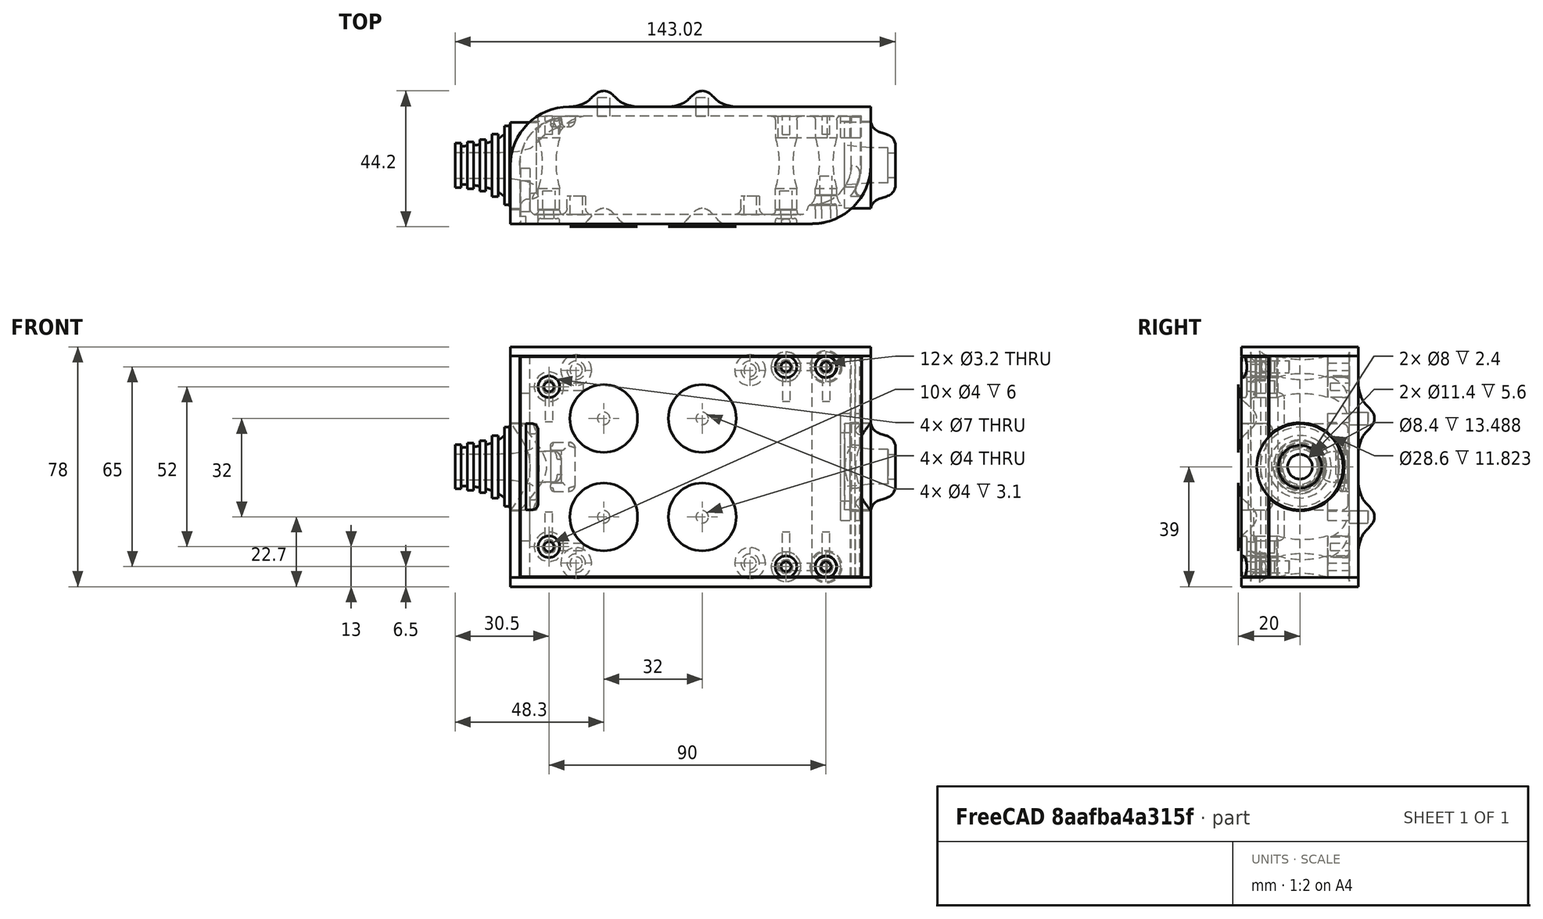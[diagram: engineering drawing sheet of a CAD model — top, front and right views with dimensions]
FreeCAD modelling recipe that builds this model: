
FCSTD DOCUMENT  (FreeCAD 0.19R0.19.2)
Label: enclosure_094
License: All rights reserved
LicenseURL: http://en.wikipedia.org/wiki/All_rights_reserved
objects: Part::Feature×72, Part::Revolution×72, Part::MultiFuse×52, Sketcher::SketchObject×29, Part::Fillet×22, Part::Cylinder×22, Part::Cut×19, Part::Extrusion×18, Part::Box×12, App::MeasureDistance×3
note: 318 computed .brp shape members not serialized (recipe doc carries the construction recipe); baked Part::Feature solids carry a one-line shape summary decoded from their .brp

FEATURE [Sketcher::SketchObject] Sketch  label="topSketch"
  FullyConstrained = true
  sketch-geometry (13):
    g0: LineSegment StartX=117 StartY=19 StartZ=0 EndX=117 EndY=38 EndZ=0
    g1: ArcOfCircle CenterX=98 CenterY=19 CenterZ=0 NormalX=0 NormalY=0 NormalZ=1 AngleXU=0 Radius=19 StartAngle=5.7297 EndAngle=6.28319
    g2: LineSegment StartX=0 StartY=3 StartZ=0 EndX=0 EndY=19 EndZ=0
    g3: LineSegment StartX=19 StartY=38 StartZ=0 EndX=117 EndY=38 EndZ=0
    g4: ArcOfCircle CenterX=19 CenterY=19 CenterZ=0 NormalX=0 NormalY=0 NormalZ=1 AngleXU=0 Radius=19 StartAngle=1.5708 EndAngle=3.14159
    g5: ArcOfCircle CenterX=19 CenterY=19 CenterZ=0 NormalX=0 NormalY=0 NormalZ=1 AngleXU=0 Radius=16 StartAngle=1.5708 EndAngle=3.14159
    g6: ArcOfCircle CenterX=98 CenterY=19 CenterZ=0 NormalX=0 NormalY=0 NormalZ=1 AngleXU=0 Radius=16 StartAngle=5.60905 EndAngle=6.28319
    g7: LineSegment StartX=114 StartY=19 StartZ=0 EndX=114 EndY=35 EndZ=0
    g8: LineSegment StartX=110.5 StartY=9.01251 StartZ=0 EndX=114.163 EndY=9.01251 EndZ=0
    g9: LineSegment StartX=114 StartY=35 StartZ=0 EndX=19 EndY=35 EndZ=0
    g10: LineSegment StartX=0 StartY=3 StartZ=0 EndX=0 EndY=0 EndZ=0
    g11: LineSegment StartX=3 StartY=0 StartZ=0 EndX=0 EndY=0 EndZ=0
    g12: LineSegment StartX=3 StartY=19 StartZ=0 EndX=3 EndY=0 EndZ=0
  constraints (33):
    c: Vertical(g0)
    c: Distance(g0) = 19
    c: Block(g0)
    c: Coincident(g1,g0)
    c: Block(g1)
    c: Vertical(g2)
    c: Block(g2)
    c: Coincident(g3,g0)
    c: Horizontal(g3)
    c: Distance(g3) = 98
    c: Coincident(g4,g3)
    c: Coincident(g4,g2)
    c: Block(g4)
    c: Coincident(g5,g4)
    c: Coincident(g6,g1)
    c: Block(g6)
    c: Block(g5)
    c: Coincident(g7,g6)
    c: Vertical(g7)
    c: Coincident(g8,g6)
    c: Coincident(g8,g1)
    c: Coincident(g9,g7)
    c: Coincident(g9,g5)
    c: Horizontal(g9)
    c: Tangent(g9,g5)
    c: Coincident(g10,g2)
    c: Distance(g10) = 3
    c: Vertical(g10)
    c: Coincident(g11,g10)
    c: Horizontal(g11)
    c: Coincident(g12,g5)
    c: Coincident(g12,g11)
    c: Vertical(g12)
FEATURE [Sketcher::SketchObject] Sketch001  label="bottomSketch"
  FullyConstrained = true
  sketch-geometry (32):
    g0: LineSegment StartX=3.3 StartY=-6.03275e-07 StartZ=0 EndX=98 EndY=-6.03275e-07 EndZ=0
    g1: ArcOfCircle CenterX=98 CenterY=19 CenterZ=0 NormalX=0 NormalY=0 NormalZ=1 AngleXU=0 Radius=19 StartAngle=4.71239 EndAngle=5.71103
    g2: LineSegment StartX=6.3 StartY=8 StartZ=0 EndX=3.3 EndY=8 EndZ=0
    g3: LineSegment StartX=3.3 StartY=8 StartZ=0 EndX=3.3 EndY=-6.03275e-07 EndZ=0
    g4: ArcOfCircle CenterX=8.3 CenterY=5 CenterZ=0 NormalX=0 NormalY=0 NormalZ=1 AngleXU=0 Radius=2 StartAngle=3.14159 EndAngle=4.71239
    g5: LineSegment StartX=6.3 StartY=8 StartZ=0 EndX=6.3 EndY=5 EndZ=0
    g6: ArcOfCircle CenterX=98 CenterY=19 CenterZ=0 NormalX=0 NormalY=0 NormalZ=1 AngleXU=0 Radius=12.7 StartAngle=4.71239 EndAngle=6.28319
    g7: LineSegment StartX=94.7 StartY=3 StartZ=0 EndX=8.3 EndY=3 EndZ=0
    g8-g12: Circle x5 (B-spline internal-alignment scaffolding for g13; pole/knot coordinates omitted)
    g13: BSplineCurve PolesCount=5 KnotsCount=3 Degree=3 IsPeriodic=0
    g14: GeomPoint X=98 Y=6.3 Z=0
    g15: GeomPoint X=96.3938 Y=4.71946 Z=0
    g16: GeomPoint X=94.7 Y=3 Z=0
    g17-g23: Circle x7 (B-spline internal-alignment scaffolding for g24; pole/knot coordinates omitted)
    g24: BSplineCurve PolesCount=7 KnotsCount=5 Degree=3 IsPeriodic=0
    g25-g29: GeomPoint x5 (B-spline internal-alignment scaffolding for g24; pole/knot coordinates omitted)
    g30: ArcOfCircle CenterX=98 CenterY=19 CenterZ=0 NormalX=0 NormalY=0 NormalZ=1 AngleXU=0 Radius=15.7 StartAngle=5.81226 EndAngle=6.28319
    g31: LineSegment StartX=110.7 StartY=19 StartZ=0 EndX=113.7 EndY=19 EndZ=0
  constraints (41):
    c: Horizontal(g0)
    c: Coincident(g1,g0)
    c: Block(g1)
    c: Horizontal(g2)
    c: Distance(g2) = 3
    c: Coincident(g3,g2)
    c: Vertical(g3)
    c: Coincident(g3,g0)
    c: Block(g4)
    c: Block(g2)
    c: Coincident(g5,g2)
    c: Coincident(g5,g4)
    c: Vertical(g5)
    c: Coincident(g6,g1)
    c: Block(g6)
    c: Coincident(g7,g4)
    c: Horizontal(g7)
    c: Block(g0)
    c: Block(g7)
    c: Block(g3)
    c: Coincident(g13,g6)
    c: Weight(g8) = 1
    c: Equal(g8, g9-g12) x4
    c: Coincident(g13,g7)
    c: InternalAlignment(g8-g12 -> g13) x5
    c: InternalAlignment(g14,g13)
    c: InternalAlignment(g15,g13)
    c: InternalAlignment(g16,g13)
    c: Block(g13)
    c: Weight(g17) = 1
    c: Equal(g17, g18-g23) x6
    c: Coincident(g24,g1)
    c: InternalAlignment(g17-g23 -> g24) x7
    c: InternalAlignment(g25-g29 -> g24) x5
    c: Block(g24)
    c: Coincident(g30,g24)
    c: Coincident(g31,g6)
    c: Coincident(g31,g30)
    c: Horizontal(g31)
    c: Block(g31)
    c: Block(g30)
FEATURE [Part::Extrusion] Extrude  label="top"
  Base = -> Sketch
  Dir = (0,0,1)
  DirMode = 2
  FaceMakerClass = Part::FaceMakerBullseye
  LengthFwd = 72
  LengthRev = 0
  Solid = true
  Symmetric = false
FEATURE [Part::Extrusion] Extrude001  label="bottom"
  Base = -> Sketch001
  Dir = (0,0,1)
  DirMode = 2
  FaceMakerClass = Part::FaceMakerBullseye
  LengthFwd = 71.4
  LengthRev = 0
  Placement = pos=(0,0,0.3) rot=(0,0,1;0rad)
  Solid = true
  Symmetric = false
FEATURE [Sketcher::SketchObject] Sketch002  label="topSketch001"
  FullyConstrained = true
  sketch-geometry (6):
    g0: LineSegment StartX=19 StartY=38 StartZ=0 EndX=117 EndY=38 EndZ=0
    g1: ArcOfCircle CenterX=19 CenterY=19 CenterZ=0 NormalX=0 NormalY=0 NormalZ=1 AngleXU=0 Radius=19 StartAngle=1.5708 EndAngle=3.14159
    g2: LineSegment StartX=117 StartY=38 StartZ=0 EndX=117 EndY=19 EndZ=0
    g3: LineSegment StartX=98 StartY=1.0161e-12 StartZ=0 EndX=5.22862e-06 EndY=1.0161e-12 EndZ=0
    g4: LineSegment StartX=5.22862e-06 StartY=19 StartZ=0 EndX=5.22862e-06 EndY=1.0161e-12 EndZ=0
    g5: ArcOfCircle CenterX=98 CenterY=19 CenterZ=0 NormalX=0 NormalY=0 NormalZ=1 AngleXU=0 Radius=19 StartAngle=4.71239 EndAngle=6.28319
  constraints (16):
    c: Horizontal(g0)
    c: Distance(g0) = 98
    c: Coincident(g1,g0)
    c: Block(g1)
    c: Coincident(g2,g0)
    c: Vertical(g2)
    c: Distance(g2) = 19
    c: Horizontal(g3)
    c: Coincident(g4,g1)
    c: Vertical(g4)
    c: Coincident(g3,g4)
    c: Block(g3)
    c: Coincident(g5,g2)
    c: Coincident(g5,g3)
    c: Block(g0)
    c: Block(g5)
FEATURE [Part::Extrusion] Extrude002  label="sideA"
  Base = -> Sketch002
  Dir = (0,0,1)
  DirMode = 2
  FaceMakerClass = Part::FaceMakerBullseye
  LengthFwd = 3
  LengthRev = 0
  Placement = pos=(0,0,-3) rot=(0,0,1;0rad)
  Solid = true
  Symmetric = false
FEATURE [Sketcher::SketchObject] Sketch003  label="topSketch002"
  FullyConstrained = true
  sketch-geometry (6):
    g0: LineSegment StartX=19 StartY=38 StartZ=0 EndX=117 EndY=38 EndZ=0
    g1: ArcOfCircle CenterX=19 CenterY=19 CenterZ=0 NormalX=0 NormalY=0 NormalZ=1 AngleXU=0 Radius=19 StartAngle=1.5708 EndAngle=3.14159
    g2: LineSegment StartX=117 StartY=38 StartZ=0 EndX=117 EndY=19 EndZ=0
    g3: LineSegment StartX=98 StartY=1.0161e-12 StartZ=0 EndX=5.22862e-06 EndY=1.0161e-12 EndZ=0
    g4: LineSegment StartX=5.22862e-06 StartY=19 StartZ=0 EndX=5.22862e-06 EndY=1.0161e-12 EndZ=0
    g5: ArcOfCircle CenterX=98 CenterY=19 CenterZ=0 NormalX=0 NormalY=0 NormalZ=1 AngleXU=0 Radius=19 StartAngle=4.71239 EndAngle=6.28319
  constraints (16):
    c: Horizontal(g0)
    c: Distance(g0) = 98
    c: Coincident(g1,g0)
    c: Block(g1)
    c: Coincident(g2,g0)
    c: Vertical(g2)
    c: Distance(g2) = 19
    c: Horizontal(g3)
    c: Coincident(g4,g1)
    c: Vertical(g4)
    c: Coincident(g3,g4)
    c: Block(g3)
    c: Coincident(g5,g2)
    c: Coincident(g5,g3)
    c: Block(g0)
    c: Block(g5)
FEATURE [Part::Extrusion] Extrude003  label="sideB"
  Base = -> Sketch003
  Dir = (0,0,1)
  DirMode = 2
  FaceMakerClass = Part::FaceMakerBullseye
  LengthFwd = 3
  LengthRev = 0
  Placement = pos=(0,0,72) rot=(0,0,1;0rad)
  Solid = true
  Symmetric = false
FEATURE [Sketcher::SketchObject] Sketch004
  FullyConstrained = true
  MapMode = 3
  Placement = pos=(0,0,0) rot=(1,0,0;1.5708rad)
  Support = -> [Extrude]
  sketch-geometry (8):
    g0: Circle CenterX=80.351 CenterY=-67.6202 CenterZ=0 NormalX=0 NormalY=0 NormalZ=1 AngleXU=0 Radius=2
    g1: Circle CenterX=80.351 CenterY=-67.6202 CenterZ=0 NormalX=0 NormalY=0 NormalZ=1 AngleXU=0 Radius=3
    g2: Circle CenterX=80.351 CenterY=-4.92017 CenterZ=0 NormalX=0 NormalY=0 NormalZ=1 AngleXU=0 Radius=2
    g3: Circle CenterX=80.351 CenterY=-4.92017 CenterZ=0 NormalX=0 NormalY=0 NormalZ=1 AngleXU=0 Radius=3
    g4: Circle CenterX=23.851 CenterY=-4.92017 CenterZ=0 NormalX=0 NormalY=0 NormalZ=1 AngleXU=0 Radius=2
    g5: Circle CenterX=23.851 CenterY=-4.92017 CenterZ=0 NormalX=0 NormalY=0 NormalZ=1 AngleXU=0 Radius=3
    g6: Circle CenterX=23.851 CenterY=-67.6202 CenterZ=0 NormalX=0 NormalY=0 NormalZ=1 AngleXU=0 Radius=2
    g7: Circle CenterX=23.851 CenterY=-67.6202 CenterZ=0 NormalX=0 NormalY=0 NormalZ=1 AngleXU=0 Radius=3
  constraints (8):
    c: Block(g3)
    c: Block(g2)
    c: Block(g1)
    c: Block(g0)
    c: Block(g6)
    c: Block(g7)
    c: Block(g4)
    c: Block(g5)
FEATURE [Part::Extrusion] Extrude004
  Base = -> Sketch004
  Dir = (0,-1,2e-16)
  DirMode = 2
  FaceMakerClass = Part::FaceMakerBullseye
  LengthFwd = 6
  LengthRev = 0
  Placement = pos=(0,9,0) rot=(0,0,1;0rad)
  Solid = true
  Symmetric = false
FEATURE [Sketcher::SketchObject] Sketch005
  FullyConstrained = true
  MapMode = 3
  Placement = pos=(0,0,0) rot=(1,0,0;1.5708rad)
  Support = -> [Extrude]
  sketch-geometry (8):
    g0: Circle CenterX=80.351 CenterY=-67.6202 CenterZ=0 NormalX=0 NormalY=0 NormalZ=1 AngleXU=0 Radius=3
    g1: Circle CenterX=80.351 CenterY=-4.92017 CenterZ=0 NormalX=0 NormalY=0 NormalZ=1 AngleXU=0 Radius=3
    g2: Circle CenterX=23.851 CenterY=-4.92017 CenterZ=0 NormalX=0 NormalY=0 NormalZ=1 AngleXU=0 Radius=3
    g3: Circle CenterX=23.851 CenterY=-67.6202 CenterZ=0 NormalX=0 NormalY=0 NormalZ=1 AngleXU=0 Radius=3
    g4: Circle CenterX=23.851 CenterY=-67.6202 CenterZ=0 NormalX=0 NormalY=0 NormalZ=1 AngleXU=0 Radius=5
    g5: Circle CenterX=80.351 CenterY=-67.6202 CenterZ=0 NormalX=0 NormalY=0 NormalZ=1 AngleXU=0 Radius=5
    g6: Circle CenterX=23.851 CenterY=-4.92017 CenterZ=0 NormalX=0 NormalY=0 NormalZ=1 AngleXU=0 Radius=5
    g7: Circle CenterX=80.351 CenterY=-4.92017 CenterZ=0 NormalX=0 NormalY=0 NormalZ=1 AngleXU=0 Radius=5
  constraints (8):
    c: Block(g1)
    c: Block(g0)
    c: Block(g3)
    c: Block(g2)
    c: Block(g5)
    c: Block(g4)
    c: Block(g6)
    c: Block(g7)
FEATURE [Part::Extrusion] Extrude005
  Base = -> Sketch005
  Dir = (0,-1,2e-16)
  DirMode = 2
  FaceMakerClass = Part::FaceMakerBullseye
  LengthFwd = 2
  LengthRev = 0
  Solid = true
  Symmetric = false
FEATURE [Sketcher::SketchObject] Sketch006
  FullyConstrained = true
  MapMode = 3
  Placement = pos=(0,0,0) rot=(1,0,0;1.5708rad)
  sketch-geometry (8):
    g0: Circle CenterX=80.351 CenterY=-67.6202 CenterZ=0 NormalX=0 NormalY=0 NormalZ=1 AngleXU=0 Radius=3
    g1: Circle CenterX=80.351 CenterY=-4.92017 CenterZ=0 NormalX=0 NormalY=0 NormalZ=1 AngleXU=0 Radius=3
    g2: Circle CenterX=23.851 CenterY=-4.92017 CenterZ=0 NormalX=0 NormalY=0 NormalZ=1 AngleXU=0 Radius=3
    g3: Circle CenterX=23.851 CenterY=-67.6202 CenterZ=0 NormalX=0 NormalY=0 NormalZ=1 AngleXU=0 Radius=3
    g4: Circle CenterX=23.851 CenterY=-67.6202 CenterZ=0 NormalX=0 NormalY=0 NormalZ=1 AngleXU=0 Radius=5
    g5: Circle CenterX=80.351 CenterY=-67.6202 CenterZ=0 NormalX=0 NormalY=0 NormalZ=1 AngleXU=0 Radius=5
    g6: Circle CenterX=23.851 CenterY=-4.92017 CenterZ=0 NormalX=0 NormalY=0 NormalZ=1 AngleXU=0 Radius=5
    g7: Circle CenterX=80.351 CenterY=-4.92017 CenterZ=0 NormalX=0 NormalY=0 NormalZ=1 AngleXU=0 Radius=5
  constraints (8):
    c: Block(g1)
    c: Block(g0)
    c: Block(g3)
    c: Block(g2)
    c: Block(g5)
    c: Block(g4)
    c: Block(g6)
    c: Block(g7)
FEATURE [Part::Extrusion] Extrude007
  Base = -> Sketch006
  Dir = (0,-1,2e-16)
  DirMode = 2
  FaceMakerClass = Part::FaceMakerBullseye
  LengthFwd = 2
  LengthRev = 0
  Solid = true
  Symmetric = false
FEATURE [Part::Fillet] Fillet
  Base = -> Extrude007
  Edges = 4 edges r=1.99: [Edge6,Edge12,Edge18,Edge24]
FEATURE [Part::Cut] Cut
  Base = -> Extrude005
  Placement = pos=(0,5,0) rot=(0,0,1;0rad)
  Tool = -> Fillet
FEATURE [Part::MultiFuse] Fusion  label="pCBScrews"
  Placement = pos=(-2.5,0,72.3) rot=(0,0,1;0rad)
  Shapes = -> [Extrude004,Cut]
FEATURE [App::MeasureDistance] Distance  label="Distance: 0.69 mm"
  Distance = 0.685967
  P1 = (24.0138,2.9647,0.3)
  P2 = (23.8901,3,-0.373787)
FEATURE [App::MeasureDistance] Distance001  label="Distance: 0.53 mm"
  Distance = 0.533607
  P1 = (80.2939,3,72.2334)
  P2 = (80.281,2.99661,71.7)
FEATURE [Part::Fillet] Fillet001
  Base = -> Extrude001
  Edges = 1 edges r=2.4: [Edge17]
FEATURE [Part::Fillet] Fillet002  label="bottom001"
  Base = -> Fillet001
  Edges = 1 edges r=2.4: [Edge36]
FEATURE [Part::Fillet] Fillet003  label="top001"
  Base = -> Extrude
  Edges = 1 edges r=2: [Edge1]
FEATURE [Sketcher::SketchObject] Sketch007
  FullyConstrained = true
  sketch-geometry (16):
    g0: LineSegment StartX=4 StartY=0 StartZ=0 EndX=4 EndY=2.4 EndZ=0
    g1: LineSegment StartX=4 StartY=2.4 StartZ=0 EndX=7 EndY=2.4 EndZ=0
    g2: LineSegment StartX=4 StartY=0 StartZ=0 EndX=5.7 EndY=0 EndZ=0
    g3: LineSegment StartX=5.7 StartY=0 StartZ=0 EndX=5.7 EndY=-5.6 EndZ=0
    g4-g8: Circle x5 (B-spline internal-alignment scaffolding for g9; pole/knot coordinates omitted)
    g9: BSplineCurve PolesCount=5 KnotsCount=3 Degree=3 IsPeriodic=0
    g10: GeomPoint X=7 Y=2.4 Z=0
    g11: GeomPoint X=10.4582 Y=-1.55472 Z=0
    g12: GeomPoint X=14 Y=-5.6 Z=0
    g13: LineSegment StartX=14 StartY=-5.6 StartZ=0 EndX=14 EndY=-14.1 EndZ=0
    g14: LineSegment StartX=14 StartY=-14.1 StartZ=0 EndX=6.5 EndY=-14.1 EndZ=0
    g15: LineSegment StartX=5.7 StartY=-5.6 StartZ=0 EndX=6.5 EndY=-14.1 EndZ=0
  constraints (28):
    c: Distance(g0) = 2.4
    c: Vertical(g0)
    c: Block(g0)
    c: Coincident(g1,g0)
    c: Horizontal(g1)
    c: Distance(g1) = 3
    c: Coincident(g2,g0)
    c: Horizontal(g2)
    c: Distance(g2) = 1.7
    c: Coincident(g3,g2)
    c: Vertical(g3)
    c: Distance(g3) = 5.6
    c: Coincident(g9,g1)
    c: Weight(g4) = 1
    c: Equal(g4, g5-g8) x4
    c: InternalAlignment(g4-g8 -> g9) x5
    c: InternalAlignment(g10,g9)
    c: InternalAlignment(g11,g9)
    c: InternalAlignment(g12,g9)
    c: Block(g9)
    c: Coincident(g13,g9)
    c: Vertical(g13)
    c: Distance(g13) = 8.5
    c: Coincident(g14,g13)
    c: Horizontal(g14)
    c: Distance(g14) = 7.5
    c: Coincident(g15,g3)
    c: Coincident(g15,g14)
FEATURE [Part::Feature] Face
  shape: bbox 10 x 16.5 x 2e-07 mm, 1 faces, 0 solids (baked)
FEATURE [Part::Revolution] Revolve  label="plugHousing"
  Angle = 360
  Axis = (0,1,0)
  Base = (0,0,0)
  FaceMakerClass = Part::FaceMakerBullseye
  Placement = pos=(0,0,36.15) rot=(0,0,1;0rad)
  Solid = false
  Source = -> Face
  Symmetric = false
FEATURE [Part::Feature] Face001
  shape: bbox 10 x 16.5 x 2e-07 mm, 1 faces, 0 solids (baked)
FEATURE [Part::Revolution] Revolve001  label="plugHousing001"
  Angle = 360
  Axis = (0,1,0)
  Base = (0,0,0)
  FaceMakerClass = Part::FaceMakerBullseye
  Placement = pos=(0,0,36.15) rot=(0,0,1;0rad)
  Solid = false
  Source = -> Face001
  Symmetric = false
FEATURE [Part::MultiFuse] Fusion001  label="plugHousing002"
  Placement = pos=(0,0,0) rot=(0,0,1;1.5708rad)
  Shapes = -> [Revolve001,Revolve]
FEATURE [Part::Feature] Face002
  shape: bbox 10 x 16.5 x 2e-07 mm, 1 faces, 0 solids (baked)
FEATURE [Part::Revolution] Revolve003  label="plugHousing005"
  Angle = 360
  Axis = (0,1,0)
  Base = (0,0,0)
  FaceMakerClass = Part::FaceMakerBullseye
  Placement = pos=(0,0,36.15) rot=(0,0,1;0rad)
  Solid = false
  Source = -> Face002
  Symmetric = false
FEATURE [Part::Feature] Face003
  shape: bbox 10 x 16.5 x 2e-07 mm, 1 faces, 0 solids (baked)
FEATURE [Part::Revolution] Revolve002  label="plugHousing003"
  Angle = 360
  Axis = (0,1,0)
  Base = (0,0,0)
  FaceMakerClass = Part::FaceMakerBullseye
  Placement = pos=(0,0,36.15) rot=(0,0,1;0rad)
  Solid = false
  Source = -> Face003
  Symmetric = false
FEATURE [Part::MultiFuse] Fusion002  label="plugHousing004"
  Placement = pos=(0,0,0) rot=(0,0,1;1.5708rad)
  Shapes = -> [Revolve002,Revolve003]
FEATURE [Part::MultiFuse] Fusion003  label="plugHousing006"
  Placement = pos=(0,19,0) rot=(0,0,1;3.14159rad)
  Shapes = -> [Fusion002,Fusion001]
FEATURE [Part::Feature] Face004
  shape: bbox 10 x 16.5 x 2e-07 mm, 1 faces, 0 solids (baked)
FEATURE [Part::Revolution] Revolve006  label="plugHousing010"
  Angle = 360
  Axis = (0,1,0)
  Base = (0,0,0)
  FaceMakerClass = Part::FaceMakerBullseye
  Placement = pos=(0,0,36.15) rot=(0,0,1;0rad)
  Solid = false
  Source = -> Face004
  Symmetric = false
FEATURE [Part::Feature] Face005
  shape: bbox 10 x 16.5 x 2e-07 mm, 1 faces, 0 solids (baked)
FEATURE [Part::Revolution] Revolve007  label="plugHousing011"
  Angle = 360
  Axis = (0,1,0)
  Base = (0,0,0)
  FaceMakerClass = Part::FaceMakerBullseye
  Placement = pos=(0,0,36.15) rot=(0,0,1;0rad)
  Solid = false
  Source = -> Face005
  Symmetric = false
FEATURE [Part::Feature] Face006
  shape: bbox 10 x 16.5 x 2e-07 mm, 1 faces, 0 solids (baked)
FEATURE [Part::Revolution] Revolve004  label="plugHousing007"
  Angle = 360
  Axis = (0,1,0)
  Base = (0,0,0)
  FaceMakerClass = Part::FaceMakerBullseye
  Placement = pos=(0,0,36.15) rot=(0,0,1;0rad)
  Solid = false
  Source = -> Face006
  Symmetric = false
FEATURE [Part::MultiFuse] Fusion004  label="plugHousing009"
  Placement = pos=(0,0,0) rot=(0,0,1;1.5708rad)
  Shapes = -> [Revolve004,Revolve007]
FEATURE [Part::Feature] Face007
  shape: bbox 10 x 16.5 x 2e-07 mm, 1 faces, 0 solids (baked)
FEATURE [Part::Revolution] Revolve005  label="plugHousing008"
  Angle = 360
  Axis = (0,1,0)
  Base = (0,0,0)
  FaceMakerClass = Part::FaceMakerBullseye
  Placement = pos=(0,0,36.15) rot=(0,0,1;0rad)
  Solid = false
  Source = -> Face007
  Symmetric = false
FEATURE [Part::MultiFuse] Fusion005  label="plugHousing012"
  Placement = pos=(0,0,0) rot=(0,0,1;1.5708rad)
  Shapes = -> [Revolve006,Revolve005]
FEATURE [Part::MultiFuse] Fusion006  label="plugHousing013"
  Placement = pos=(0,19,0) rot=(0,0,1;3.14159rad)
  Shapes = -> [Fusion005,Fusion004]
FEATURE [Part::MultiFuse] Fusion007  label="plugHousing014"
  Placement = pos=(122.621,0,-0.15) rot=(0,0,1;0rad)
  Shapes = -> [Fusion003,Fusion006]
FEATURE [Part::Cylinder] Cylinder002
  Angle = 360
  AttacherType = Attacher::AttachEngine3D
  Height = 20
  Placement = pos=(0,0,36.15) rot=(0,0,1;0rad)
  Radius = 4
FEATURE [Part::Cylinder] Cylinder003
  Angle = 360
  AttacherType = Attacher::AttachEngine3D
  Height = 10
  Placement = pos=(0,0,36.15) rot=(0,0,1;0rad)
  Radius = 4
FEATURE [Part::MultiFuse] Fusion009  label="removeToCreateHoleForPlugHousing"
  Placement = pos=(70,19,36.15) rot=(0,1,0;1.5708rad)
  Shapes = -> [Cylinder002,Cylinder003]
FEATURE [Part::Cylinder] Cylinder004
  Angle = 360
  AttacherType = Attacher::AttachEngine3D
  Height = 20
  Placement = pos=(0,0,36.15) rot=(0,0,1;0rad)
  Radius = 4
FEATURE [Part::Cylinder] Cylinder005
  Angle = 360
  AttacherType = Attacher::AttachEngine3D
  Height = 10
  Placement = pos=(0,0,36.15) rot=(0,0,1;0rad)
  Radius = 4
FEATURE [Part::MultiFuse] Fusion010  label="removeToCreateHoleForPlugHousing001"
  Placement = pos=(70,19,36.15) rot=(0,1,0;1.5708rad)
  Shapes = -> [Cylinder004,Cylinder005]
FEATURE [Part::Cut] Cut001
  Base = -> Fillet003
  Tool = -> Fusion010
FEATURE [Part::Cut] Cut002  label="Bottom"
  Base = -> Fillet002
  Tool = -> Fusion009
FEATURE [Part::Feature] Face008
  shape: bbox 10 x 16.5 x 2e-07 mm, 1 faces, 0 solids (baked)
FEATURE [Part::Revolution] Revolve011  label="plugHousing021"
  Angle = 360
  Axis = (0,1,0)
  Base = (0,0,0)
  FaceMakerClass = Part::FaceMakerBullseye
  Placement = pos=(0,0,36.15) rot=(0,0,1;0rad)
  Solid = false
  Source = -> Face008
  Symmetric = false
FEATURE [Part::Feature] Face009
  shape: bbox 10 x 16.5 x 2e-07 mm, 1 faces, 0 solids (baked)
FEATURE [Part::Revolution] Revolve012  label="plugHousing022"
  Angle = 360
  Axis = (0,1,0)
  Base = (0,0,0)
  FaceMakerClass = Part::FaceMakerBullseye
  Placement = pos=(0,0,36.15) rot=(0,0,1;0rad)
  Solid = false
  Source = -> Face009
  Symmetric = false
FEATURE [Part::Feature] Face010 .. Face013  x4 (patterned run collapsed; names and placements below)
  shape: bbox 10 x 16.5 x 2e-07 mm, 1 faces, 0 solids (baked)
FEATURE [Part::Revolution] Revolve015  label="plugHousing027"
  Angle = 360
  Axis = (0,1,0)
  Base = (0,0,0)
  FaceMakerClass = Part::FaceMakerBullseye
  Placement = pos=(0,0,36.15) rot=(0,0,1;0rad)
  Solid = false
  Source = -> Face013
  Symmetric = false
FEATURE [Part::Feature] Face014
  shape: bbox 10 x 16.5 x 2e-07 mm, 1 faces, 0 solids (baked)
FEATURE [Part::Feature] Face015
  shape: bbox 10 x 16.5 x 2e-07 mm, 1 faces, 0 solids (baked)
FEATURE [Part::Feature] Face016
  shape: bbox 10 x 16.5 x 2e-07 mm, 1 faces, 0 solids (baked)
FEATURE [Part::Revolution] Revolve019  label="plugHousing033"
  Angle = 360
  Axis = (0,1,0)
  Base = (0,0,0)
  FaceMakerClass = Part::FaceMakerBullseye
  Placement = pos=(0,0,36.15) rot=(0,0,1;0rad)
  Solid = false
  Source = -> Face016
  Symmetric = false
FEATURE [Part::Feature] Face017
  shape: bbox 10 x 16.5 x 2e-07 mm, 1 faces, 0 solids (baked)
FEATURE [Part::Revolution] Revolve020  label="plugHousing034"
  Angle = 360
  Axis = (0,1,0)
  Base = (0,0,0)
  FaceMakerClass = Part::FaceMakerBullseye
  Placement = pos=(0,0,36.15) rot=(0,0,1;0rad)
  Solid = false
  Source = -> Face017
  Symmetric = false
FEATURE [Part::Feature] Face018
  shape: bbox 10 x 16.5 x 2e-07 mm, 1 faces, 0 solids (baked)
FEATURE [Part::Revolution] Revolve016  label="plugHousing030"
  Angle = 360
  Axis = (0,1,0)
  Base = (0,0,0)
  FaceMakerClass = Part::FaceMakerBullseye
  Placement = pos=(0,0,36.15) rot=(0,0,1;0rad)
  Solid = false
  Source = -> Face018
  Symmetric = false
FEATURE [Part::MultiFuse] Fusion020  label="plugHousing038"
  Placement = pos=(0,0,0) rot=(0,0,1;1.5708rad)
  Shapes = -> [Revolve016,Revolve020]
FEATURE [Part::Feature] Face019
  shape: bbox 10 x 16.5 x 2e-07 mm, 1 faces, 0 solids (baked)
FEATURE [Part::Feature] Face020
  shape: bbox 10 x 16.5 x 2e-07 mm, 1 faces, 0 solids (baked)
FEATURE [Part::Revolution] Revolve017  label="plugHousing031"
  Angle = 360
  Axis = (0,1,0)
  Base = (0,0,0)
  FaceMakerClass = Part::FaceMakerBullseye
  Placement = pos=(0,0,36.15) rot=(0,0,1;0rad)
  Solid = false
  Source = -> Face020
  Symmetric = false
FEATURE [Part::MultiFuse] Fusion021  label="plugHousing039"
  Placement = pos=(0,0,0) rot=(0,0,1;1.5708rad)
  Shapes = -> [Revolve019,Revolve017]
FEATURE [Part::MultiFuse] Fusion023  label="plugHousing041"
  Placement = pos=(0,19,0) rot=(0,0,1;3.14159rad)
  Shapes = -> [Fusion021,Fusion020]
FEATURE [Part::Revolution] Revolve022  label="plugHousing043"
  Angle = 360
  Axis = (0,1,0)
  Base = (0,0,0)
  FaceMakerClass = Part::FaceMakerBullseye
  Placement = pos=(0,0,36.15) rot=(0,0,1;0rad)
  Solid = false
  Source = -> Face019
  Symmetric = false
FEATURE [Part::Feature] Face021
  shape: bbox 10 x 16.5 x 2e-07 mm, 1 faces, 0 solids (baked)
FEATURE [Part::Revolution] Revolve023  label="plugHousing044"
  Angle = 360
  Axis = (0,1,0)
  Base = (0,0,0)
  FaceMakerClass = Part::FaceMakerBullseye
  Placement = pos=(0,0,36.15) rot=(0,0,1;0rad)
  Solid = false
  Source = -> Face021
  Symmetric = false
FEATURE [Part::Feature] Face022
  shape: bbox 10 x 16.5 x 2e-07 mm, 1 faces, 0 solids (baked)
FEATURE [Part::Revolution] Revolve018  label="plugHousing032"
  Angle = 360
  Axis = (0,1,0)
  Base = (0,0,0)
  FaceMakerClass = Part::FaceMakerBullseye
  Placement = pos=(0,0,36.15) rot=(0,0,1;0rad)
  Solid = false
  Source = -> Face022
  Symmetric = false
FEATURE [Part::MultiFuse] Fusion022  label="plugHousing040"
  Placement = pos=(0,0,0) rot=(0,0,1;1.5708rad)
  Shapes = -> [Revolve018,Revolve023]
FEATURE [Part::Feature] Face023
  shape: bbox 10 x 16.5 x 2e-07 mm, 1 faces, 0 solids (baked)
FEATURE [Part::Revolution] Revolve021  label="plugHousing035"
  Angle = 360
  Axis = (0,1,0)
  Base = (0,0,0)
  FaceMakerClass = Part::FaceMakerBullseye
  Placement = pos=(0,0,36.15) rot=(0,0,1;0rad)
  Solid = false
  Source = -> Face023
  Symmetric = false
FEATURE [Part::MultiFuse] Fusion018  label="plugHousing036"
  Placement = pos=(0,0,0) rot=(0,0,1;1.5708rad)
  Shapes = -> [Revolve022,Revolve021]
FEATURE [Part::MultiFuse] Fusion019  label="plugHousing037"
  Placement = pos=(0,19,0) rot=(0,0,1;3.14159rad)
  Shapes = -> [Fusion018,Fusion022]
FEATURE [Part::MultiFuse] Fusion024  label="plugHousing042"
  Placement = pos=(122.621,0,-0.15) rot=(0,0,1;0rad)
  Shapes = -> [Fusion023,Fusion019]
FEATURE [Part::Cylinder] Cylinder006
  Angle = 360
  AttacherType = Attacher::AttachEngine3D
  Height = 20
  Placement = pos=(0,0,36.15) rot=(0,0,1;0rad)
  Radius = 14.3
FEATURE [Part::Cylinder] Cylinder007
  Angle = 360
  AttacherType = Attacher::AttachEngine3D
  Height = 10
  Placement = pos=(0,0,36.15) rot=(0,0,1;0rad)
  Radius = 4
FEATURE [Part::MultiFuse] Fusion026  label="removeToCreteHoleForPlugHousing"
  Placement = pos=(70,19,36) rot=(0,1,0;1.5708rad)
  Shapes = -> [Cylinder006,Cylinder007]
FEATURE [Part::Box] Box001  label="Cube001"
  AttacherType = Attacher::AttachEngine3D
  Height = 28
  Length = 3
  Placement = pos=(110.7,19,22) rot=(0,0,1;0rad)
  Width = 15.7
FEATURE [Part::Cut] Cut003  label="top002"
  Base = -> Cut001
  Tool = -> Fusion007
FEATURE [Part::Revolution] Revolve008  label="plugHousing015"
  Angle = 360
  Axis = (0,1,0)
  Base = (0,0,0)
  FaceMakerClass = Part::FaceMakerBullseye
  Placement = pos=(0,0,36.15) rot=(0,0,1;0rad)
  Solid = false
  Source = -> Face010
  Symmetric = false
FEATURE [Part::MultiFuse] Fusion013  label="plugHousing020"
  Placement = pos=(0,0,0) rot=(0,0,1;1.5708rad)
  Shapes = -> [Revolve008,Revolve012]
FEATURE [Part::Cut] Cut004  label="top003"
  Base = -> Cut003
  Placement = pos=(1,0,0) rot=(0,0,1;0rad)
  Tool = -> Fusion026
FEATURE [Part::Cylinder] Cylinder008
  Angle = 360
  AttacherType = Attacher::AttachEngine3D
  Height = 20
  Placement = pos=(0,0,36.15) rot=(0,0,1;0rad)
  Radius = 10.3
FEATURE [Part::Cylinder] Cylinder009
  Angle = 360
  AttacherType = Attacher::AttachEngine3D
  Height = 10
  Placement = pos=(0,0,36.15) rot=(0,0,1;0rad)
  Radius = 4
FEATURE [Part::MultiFuse] Fusion027  label="removeToCreteHoleForPlugHousing001"
  Placement = pos=(70,19,36) rot=(0,1,0;1.5708rad)
  Shapes = -> [Cylinder008,Cylinder009]
FEATURE [Part::Cut] Cut005  label="plugHousingTab"
  Base = -> Box001
  Tool = -> Fusion027
FEATURE [Part::MultiFuse] Fusion028  label="plugHousing045"
  Shapes = -> [Fusion024,Cut005]
FEATURE [Part::Box] Box002  label="Cube002"
  AttacherType = Attacher::AttachEngine3D
  Height = 28.8
  Length = 3
  Placement = pos=(107.3,28,21.6) rot=(0,0,1;0rad)
  Width = 7
FEATURE [Part::Box] Box003  label="Cube003"
  AttacherType = Attacher::AttachEngine3D
  Height = 3
  Length = 6.4
  Placement = pos=(107.3,28,18.6) rot=(0,0,1;0rad)
  Width = 7
FEATURE [Part::Box] Box004  label="Cube004"
  AttacherType = Attacher::AttachEngine3D
  Height = 3
  Length = 6.4
  Placement = pos=(107.3,28,50.4) rot=(0,0,1;0rad)
  Width = 7
FEATURE [Part::MultiFuse] Fusion029  label="plugHousingBracketHolder"
  Shapes = -> [Box004,Box002,Box003]
FEATURE [Part::Cylinder] Cylinder010
  Angle = 360
  AttacherType = Attacher::AttachEngine3D
  Height = 20
  Placement = pos=(0,0,36.15) rot=(0,0,1;0rad)
  Radius = 14.3
FEATURE [Part::Cylinder] Cylinder011
  Angle = 360
  AttacherType = Attacher::AttachEngine3D
  Height = 10
  Placement = pos=(0,0,36.15) rot=(0,0,1;0rad)
  Radius = 4
FEATURE [Part::MultiFuse] Fusion030  label="removeToCreteHoleForPlugHousing002"
  Placement = pos=(70,19,36) rot=(0,1,0;1.5708rad)
  Shapes = -> [Cylinder010,Cylinder011]
FEATURE [Part::Cut] Cut006  label="plugHousingBracketHolder001"
  Base = -> Fusion029
  Tool = -> Fusion030
FEATURE [Part::Cylinder] Cylinder012
  Angle = 360
  AttacherType = Attacher::AttachEngine3D
  Height = 20
  Placement = pos=(0,0,36.15) rot=(0,0,1;0rad)
  Radius = 7
FEATURE [Part::Cylinder] Cylinder013
  Angle = 360
  AttacherType = Attacher::AttachEngine3D
  Height = 10
  Placement = pos=(0,0,36.15) rot=(0,0,1;0rad)
  Radius = 4
FEATURE [Part::MultiFuse] Fusion032  label="removeToCreteHoleForPlugHousing003"
  Placement = pos=(70,19,36) rot=(0,1,0;1.5708rad)
  Shapes = -> [Cylinder012,Cylinder013]
FEATURE [Part::Cut] Cut007  label="bottom002"
  Base = -> Cut002
  Tool = -> Fusion032
FEATURE [Sketcher::SketchObject] Sketch008
  FullyConstrained = true
  sketch-geometry (54):
    g0: LineSegment StartX=-4.2 StartY=0 StartZ=0 EndX=-6.2 EndY=0 EndZ=0
    g1: LineSegment StartX=-14 StartY=-18 StartZ=0 EndX=-14 EndY=-26.5 EndZ=0
    g2: LineSegment StartX=-4.2 StartY=0 StartZ=0 EndX=-4.2 EndY=-13.4877 EndZ=0
    g3: Circle CenterX=-4.2 CenterY=-13.4877 CenterZ=0 NormalX=0 NormalY=0 NormalZ=1 AngleXU=0 Radius=1
    g4: Circle CenterX=-4.2 CenterY=-26.5 CenterZ=0 NormalX=0 NormalY=0 NormalZ=1 AngleXU=0 Radius=1
    g5: Circle CenterX=-8.2 CenterY=-26.5 CenterZ=0 NormalX=0 NormalY=0 NormalZ=1 AngleXU=0 Radius=1
    g6: BSplineCurve PolesCount=3 KnotsCount=2 Degree=2 IsPeriodic=0
    g7: GeomPoint X=-4.2 Y=-13.4877 Z=0
    g8: GeomPoint X=-8.2 Y=-26.5 Z=0
    g9: LineSegment StartX=-14 StartY=-26.5 StartZ=0 EndX=-8.2 EndY=-26.5 EndZ=0
    g10: LineSegment StartX=-10.15 StartY=-12 StartZ=0 EndX=-10.15 EndY=-14 EndZ=0
    g11: LineSegment StartX=-12.8401 StartY=-16 StartZ=0 EndX=-10.1571 EndY=-16 EndZ=0
    g12: LineSegment StartX=-10.15 StartY=-14 StartZ=0 EndX=-8.70761 EndY=-14 EndZ=0
    g13: LineSegment StartX=-12.8401 StartY=-16 StartZ=0 EndX=-12.8401 EndY=-17.6958 EndZ=0
    g14: LineSegment StartX=-10.15 StartY=-12 StartZ=0 EndX=-7.79258 EndY=-12 EndZ=0
    g15: Circle CenterX=-6.2215 CenterY=-2 CenterZ=0 NormalX=0 NormalY=0 NormalZ=1 AngleXU=0 Radius=1
    g16: Circle CenterX=-6.22762 CenterY=-2.58724 CenterZ=0 NormalX=0 NormalY=0 NormalZ=1 AngleXU=0 Radius=1
    g17: Circle CenterX=-6.32538 CenterY=-4 CenterZ=0 NormalX=0 NormalY=0 NormalZ=1 AngleXU=0 Radius=1
    g18: BSplineCurve PolesCount=3 KnotsCount=2 Degree=2 IsPeriodic=0
    g19: GeomPoint X=-6.2215 Y=-2 Z=0
    g20: GeomPoint X=-6.32538 Y=-4 Z=0
    g21: Circle CenterX=-6.48644 CenterY=-5.99526 CenterZ=0 NormalX=0 NormalY=0 NormalZ=1 AngleXU=0 Radius=1
    g22: Circle CenterX=-6.58486 CenterY=-6.99526 CenterZ=0 NormalX=0 NormalY=0 NormalZ=1 AngleXU=0 Radius=1
    g23: Circle CenterX=-6.77343 CenterY=-8 CenterZ=0 NormalX=0 NormalY=0 NormalZ=1 AngleXU=0 Radius=1
    g24: BSplineCurve PolesCount=3 KnotsCount=2 Degree=2 IsPeriodic=0
    g25: GeomPoint X=-6.48644 Y=-5.99526 Z=0
    g26: GeomPoint X=-6.77343 Y=-8 Z=0
    g27: Circle CenterX=-7.19003 CenterY=-10 CenterZ=0 NormalX=0 NormalY=0 NormalZ=1 AngleXU=0 Radius=1
    g28: Circle CenterX=-7.44407 CenterY=-11.0915 CenterZ=0 NormalX=0 NormalY=0 NormalZ=1 AngleXU=0 Radius=1
    g29: Circle CenterX=-7.79258 CenterY=-12 CenterZ=0 NormalX=0 NormalY=0 NormalZ=1 AngleXU=0 Radius=1
    g30: BSplineCurve PolesCount=3 KnotsCount=2 Degree=2 IsPeriodic=0
    g31: GeomPoint X=-7.19003 Y=-10 Z=0
    g32: GeomPoint X=-7.79258 Y=-12 Z=0
    g33: Circle CenterX=-8.70761 CenterY=-14 CenterZ=0 NormalX=0 NormalY=0 NormalZ=1 AngleXU=0 Radius=1
    g34: Circle CenterX=-9.33087 CenterY=-15.1837 CenterZ=0 NormalX=0 NormalY=0 NormalZ=1 AngleXU=0 Radius=1
    g35: Circle CenterX=-10.1571 CenterY=-16 CenterZ=0 NormalX=0 NormalY=0 NormalZ=1 AngleXU=0 Radius=1
    g36: BSplineCurve PolesCount=3 KnotsCount=2 Degree=2 IsPeriodic=0
    g37: GeomPoint X=-8.70761 Y=-14 Z=0
    g38: GeomPoint X=-10.1571 Y=-16 Z=0
    g39: Circle CenterX=-12.8401 CenterY=-17.6958 CenterZ=0 NormalX=0 NormalY=0 NormalZ=1 AngleXU=0 Radius=1
    g40: Circle CenterX=-13.3521 CenterY=-17.9027 CenterZ=0 NormalX=0 NormalY=0 NormalZ=1 AngleXU=0 Radius=1
    g41: Circle CenterX=-14 CenterY=-18 CenterZ=0 NormalX=0 NormalY=0 NormalZ=1 AngleXU=0 Radius=1
    g42: BSplineCurve PolesCount=3 KnotsCount=2 Degree=2 IsPeriodic=0
    g43: GeomPoint X=-12.8401 Y=-17.6958 Z=0
    g44: GeomPoint X=-14 Y=-18 Z=0
    g45: LineSegment StartX=-6.2 StartY=0 StartZ=0 EndX=-7.2 EndY=0 EndZ=0
    g46: LineSegment StartX=-7.2 StartY=0 StartZ=0 EndX=-7.2 EndY=-2 EndZ=0
    g47: LineSegment StartX=-7.2 StartY=-2 StartZ=0 EndX=-6.2215 EndY=-2 EndZ=0
    g48: LineSegment StartX=-6.32538 StartY=-4 StartZ=0 EndX=-7.65538 EndY=-4 EndZ=0
    g49: LineSegment StartX=-7.65538 StartY=-4 StartZ=0 EndX=-7.65538 EndY=-5.99526 EndZ=0
    g50: LineSegment StartX=-7.65538 StartY=-5.99526 StartZ=0 EndX=-6.48644 EndY=-5.99526 EndZ=0
    g51: LineSegment StartX=-6.77343 StartY=-8 StartZ=0 EndX=-8.43343 EndY=-8 EndZ=0
    g52: LineSegment StartX=-8.43343 StartY=-8 StartZ=0 EndX=-8.43343 EndY=-10 EndZ=0
    g53: LineSegment StartX=-8.43343 StartY=-10 StartZ=0 EndX=-7.19003 EndY=-10 EndZ=0
  constraints (112):
    c: Horizontal(g0)
    c: Distance(g0) = 2
    c: Block(g0)
    c: Vertical(g1)
    c: Coincident(g2,g0)
    c: Vertical(g2)
    c: Block(g2)
    c: Coincident(g6,g2)
    c: Weight(g3) = 1
    c: Equal(g3,g4)
    c: Equal(g3,g5)
    c: InternalAlignment(g3,g6)
    c: InternalAlignment(g4,g6)
    c: InternalAlignment(g5,g6)
    c: InternalAlignment(g7,g6)
    c: InternalAlignment(g8,g6)
    c: Block(g6)
    c: Coincident(g9,g1)
    c: Coincident(g9,g6)
    c: Horizontal(g9)
    c: Vertical(g10)
    c: Block(g10)
    c: Horizontal(g11)
    c: Block(g11)
    c: Coincident(g12,g10)
    c: Horizontal(g12)
    c: Block(g12)
    c: Coincident(g13,g11)
    c: Vertical(g13)
    c: Block(g13)
    c: Coincident(g14,g10)
    c: Horizontal(g14)
    c: Block(g14)
    c: Block(g9)
    c: Block(g1)
    c: Weight(g15) = 1
    c: Equal(g15,g16)
    c: Equal(g15,g17)
    c: InternalAlignment(g15,g18)
    c: InternalAlignment(g16,g18)
    c: InternalAlignment(g17,g18)
    c: InternalAlignment(g19,g18)
    c: InternalAlignment(g20,g18)
    c: Weight(g21) = 1
    c: Equal(g21,g22)
    c: Equal(g21,g23)
    c: InternalAlignment(g21,g24)
    c: InternalAlignment(g22,g24)
    c: InternalAlignment(g23,g24)
    c: InternalAlignment(g25,g24)
    c: InternalAlignment(g26,g24)
    c: Weight(g27) = 1
    c: Equal(g27,g28)
    c: Equal(g27,g29)
    c: Coincident(g30,g14)
    c: InternalAlignment(g27,g30)
    c: InternalAlignment(g28,g30)
    c: InternalAlignment(g29,g30)
    c: InternalAlignment(g31,g30)
    c: InternalAlignment(g32,g30)
    c: Coincident(g36,g12)
    c: Weight(g33) = 1
    c: Equal(g33,g34)
    c: Equal(g33,g35)
    c: Coincident(g36,g11)
    c: InternalAlignment(g33,g36)
    c: InternalAlignment(g34,g36)
    c: InternalAlignment(g35,g36)
    c: InternalAlignment(g37,g36)
    c: InternalAlignment(g38,g36)
    c: Coincident(g42,g13)
    c: Weight(g39) = 1
    c: Equal(g39,g40)
    c: Equal(g39,g41)
    c: Coincident(g42,g1)
    c: InternalAlignment(g39,g42)
    c: InternalAlignment(g40,g42)
    c: InternalAlignment(g41,g42)
    c: InternalAlignment(g43,g42)
    c: InternalAlignment(g44,g42)
    c: Block(g18)
    c: Block(g24)
    c: Block(g30)
    c: Block(g36)
    c: Block(g42)
    c: Horizontal(g45)
    c: Coincident(g45,g0)
    c: Vertical(g46)
    c: Coincident(g46,g45)
    c: Coincident(g47,g46)
    c: Coincident(g47,g18)
    c: Horizontal(g47)
    c: Block(g46)
    c: Coincident(g48,g18)
    c: Horizontal(g48)
    c: Distance(g48) = 1.33
    c: Vertical(g49)
    c: Coincident(g49,g48)
    c: Coincident(g50,g49)
    c: Coincident(g50,g24)
    c: Horizontal(g50)
    c: Tangent(g50,g22)
    c: Horizontal(g51)
    c: Coincident(g51,g24)
    c: Block(g51)
    c: Vertical(g52)
    c: Block(g52)
    c: Coincident(g52,g51)
    c: Coincident(g53,g52)
    c: Coincident(g53,g30)
    c: Horizontal(g53)
    c: Distance(g1) = 8.5
FEATURE [Part::Feature] Face024
  shape: bbox 9.8 x 26.5 x 2e-07 mm, 1 faces, 0 solids (baked)
FEATURE [Part::Revolution] Revolve024
  Angle = 360
  Axis = (0,1,0)
  Base = (0,0,0)
  FaceMakerClass = Part::FaceMakerBullseye
  Placement = pos=(0,0,0) rot=(0,0,1;1.5708rad)
  Solid = false
  Source = -> Face024
  Symmetric = false
FEATURE [Part::Feature] Face025
  shape: bbox 9.8 x 26.5 x 2e-07 mm, 1 faces, 0 solids (baked)
FEATURE [Part::Revolution] Revolve025
  Angle = 360
  Axis = (0,1,0)
  Base = (0,0,0)
  FaceMakerClass = Part::FaceMakerBullseye
  Placement = pos=(0,0,0) rot=(0,0,1;1.5708rad)
  Solid = false
  Source = -> Face025
  Symmetric = false
FEATURE [Part::MultiFuse] Fusion033
  Placement = pos=(-18,19,36) rot=(0,0,1;0rad)
  Shapes = -> [Revolve025,Revolve024]
FEATURE [Part::Cylinder] Cylinder014
  Angle = 360
  AttacherType = Attacher::AttachEngine3D
  Height = 20
  Placement = pos=(0,0,36.15) rot=(0,0,1;0rad)
  Radius = 14.3
FEATURE [Part::Cylinder] Cylinder015
  Angle = 360
  AttacherType = Attacher::AttachEngine3D
  Height = 10
  Placement = pos=(0,0,36.15) rot=(0,0,1;0rad)
  Radius = 4
FEATURE [Part::MultiFuse] Fusion034  label="removeToCreteHoleForPlugHousing004"
  Placement = pos=(-42,19,36) rot=(0,1,0;1.5708rad)
  Shapes = -> [Cylinder014,Cylinder015]
FEATURE [Part::Cut] Cut008  label="top004"
  Base = -> Cut004
  Placement = pos=(-1,0,0) rot=(0,0,1;0rad)
  Tool = -> Fusion034
FEATURE [Part::Box] Box005  label="Cube005"
  AttacherType = Attacher::AttachEngine3D
  Height = 28
  Length = 3
  Placement = pos=(110.7,19,22) rot=(0,0,1;0rad)
  Width = 15.7
FEATURE [Part::Cylinder] Cylinder016
  Angle = 360
  AttacherType = Attacher::AttachEngine3D
  Height = 10
  Placement = pos=(0,0,36.15) rot=(0,0,1;0rad)
  Radius = 4
FEATURE [Part::Cylinder] Cylinder017
  Angle = 360
  AttacherType = Attacher::AttachEngine3D
  Height = 20
  Placement = pos=(0,0,36.15) rot=(0,0,1;0rad)
  Radius = 10.3
FEATURE [Part::MultiFuse] Fusion035  label="removeToCreteHoleForPlugHousing005"
  Placement = pos=(70,19,36) rot=(0,1,0;1.5708rad)
  Shapes = -> [Cylinder017,Cylinder016]
FEATURE [Part::Cut] Cut009  label="plugHousingTab001"
  Base = -> Box005
  Placement = pos=(-107.4,-14,0) rot=(0,0,1;0rad)
  Tool = -> Fusion035
FEATURE [Part::Box] Box006  label="Cube006"
  AttacherType = Attacher::AttachEngine3D
  Height = 28
  Length = 3
  Placement = pos=(110.7,19,22) rot=(0,0,1;0rad)
  Width = 15.7
FEATURE [Part::Cylinder] Cylinder018
  Angle = 360
  AttacherType = Attacher::AttachEngine3D
  Height = 10
  Placement = pos=(0,0,36.15) rot=(0,0,1;0rad)
  Radius = 4
FEATURE [Part::Cylinder] Cylinder019
  Angle = 360
  AttacherType = Attacher::AttachEngine3D
  Height = 20
  Placement = pos=(0,0,36.15) rot=(0,0,1;0rad)
  Radius = 10.3
FEATURE [Part::MultiFuse] Fusion036  label="removeToCreteHoleForPlugHousing006"
  Placement = pos=(70,19,36) rot=(0,1,0;1.5708rad)
  Shapes = -> [Cylinder019,Cylinder018]
FEATURE [Part::Cut] Cut010  label="plugHousingTab002"
  Base = -> Box006
  Placement = pos=(-107.4,-14,0) rot=(0,0,1;0rad)
  Tool = -> Fusion036
FEATURE [Part::MultiFuse] Fusion037
  Placement = pos=(9.6,23,0) rot=(0,0,1;3.14159rad)
  Shapes = -> [Cut009,Cut010]
FEATURE [Part::Box] Box  label="Cube"
  AttacherType = Attacher::AttachEngine3D
  Height = 10
  Length = 3
  Placement = pos=(3.3,4,12) rot=(0,0,1;0rad)
  Width = 10
FEATURE [Part::Fillet] Fillet004
  Base = -> Fusion028
  Edges = 1 edges r=2: [Edge25]
FEATURE [Part::Fillet] Fillet005  label="plugHousing046"
  Base = -> Fillet004
  Edges = 1 edges r=2: [Edge8]
FEATURE [Part::Fillet] Fillet006
  Base = -> Box
  Edges = 1 edges r=2: [Edge11]
FEATURE [Part::Box] Box007  label="Cube007"
  AttacherType = Attacher::AttachEngine3D
  Height = 10
  Length = 3
  Placement = pos=(3.3,4,50) rot=(0,0,1;0rad)
  Width = 10
FEATURE [Part::Fillet] Fillet007
  Base = -> Box007
  Edges = 1 edges r=2: [Edge12]
FEATURE [Part::Box] Box008  label="Cube008"
  AttacherType = Attacher::AttachEngine3D
  Height = 28
  Length = 4
  Placement = pos=(5,0,22) rot=(0,0,1;0rad)
  Width = 10
FEATURE [Part::Fillet] Fillet008
  Base = -> Box008
  Edges = 1 edges r=1: [Edge7]
FEATURE [Part::Fillet] Fillet009
  Base = -> Fillet008
  Edges = 1 edges r=2: [Edge5]
FEATURE [Part::Fillet] Fillet010
  Base = -> Fillet009
  Edges = 1 edges r=2: [Edge2]
FEATURE [Sketcher::SketchObject] Sketch009  label="topSketch003"
  FullyConstrained = true
  sketch-geometry (4):
    g0: LineSegment StartX=16.8446 StartY=31.512 StartZ=0 EndX=16.3251 EndY=34.4666 EndZ=0
    g1: ArcOfCircle CenterX=19 CenterY=19.2524 CenterZ=0 NormalX=0 NormalY=0 NormalZ=1 AngleXU=0 Radius=15.4476 StartAngle=1.74483 EndAngle=2.72717
    g2: ArcOfCircle CenterX=19 CenterY=19.2524 CenterZ=0 NormalX=0 NormalY=0 NormalZ=1 AngleXU=0 Radius=12.4476 StartAngle=1.74483 EndAngle=2.73189
    g3: LineSegment StartX=4.86004 StartY=25.4725 StartZ=0 EndX=7.58253 EndY=24.2107 EndZ=0
  constraints (7):
    c: Block(g0)
    c: Coincident(g1,g0)
    c: Coincident(g2,g0)
    c: Coincident(g3,g1)
    c: Coincident(g3,g2)
    c: Block(g1)
    c: Block(g2)
FEATURE [Part::Extrusion] Extrude008
  Base = -> Sketch009
  Dir = (0,0,1)
  DirMode = 2
  FaceMakerClass = Part::FaceMakerBullseye
  LengthFwd = 10
  LengthRev = 0
  Placement = pos=(0,0,31) rot=(0,0,1;0rad)
  Solid = true
  Symmetric = false
FEATURE [Part::Cylinder] Cylinder020
  Angle = 360
  AttacherType = Attacher::AttachEngine3D
  Height = 20
  Placement = pos=(0,0,36.15) rot=(0,0,1;0rad)
  Radius = 8.2
FEATURE [Part::Cylinder] Cylinder021
  Angle = 360
  AttacherType = Attacher::AttachEngine3D
  Height = 10
  Placement = pos=(0,0,36.15) rot=(0,0,1;0rad)
  Radius = 4
FEATURE [Part::MultiFuse] Fusion038  label="removeToCreteHoleForPlugHousing007"
  Placement = pos=(-42,19,36) rot=(0,1,0;1.5708rad)
  Shapes = -> [Cylinder020,Cylinder021]
FEATURE [Part::Cut] Cut011
  Base = -> Extrude008
  Tool = -> Fusion038
FEATURE [Part::Fillet] Fillet011
  Base = -> Cut011
  Edges = 1 edges r=2: [Edge1]
FEATURE [Part::Fillet] Fillet012
  Base = -> Fillet011
  Edges = 1 edges r=2.5: [Edge1]
FEATURE [Part::Fillet] Fillet013
  Base = -> Fillet012
  Edges = 1 edges r=2.5: [Edge2]
FEATURE [Part::Box] Box010  label="Cube010"
  AttacherType = Attacher::AttachEngine3D
  Height = 16
  Length = 8
  Placement = pos=(12.7,31.52,28) rot=(0,0,1;0rad)
  Width = 4
FEATURE [Sketcher::SketchObject] Sketch010  label="topSketch004"
  FullyConstrained = true
  sketch-geometry (4):
    g0: LineSegment StartX=16.8446 StartY=31.512 StartZ=0 EndX=16.3251 EndY=34.4666 EndZ=0
    g1: ArcOfCircle CenterX=19 CenterY=19.2524 CenterZ=0 NormalX=0 NormalY=0 NormalZ=1 AngleXU=0 Radius=15.4476 StartAngle=1.74483 EndAngle=2.72717
    g2: ArcOfCircle CenterX=19 CenterY=19.2524 CenterZ=0 NormalX=0 NormalY=0 NormalZ=1 AngleXU=0 Radius=12.4476 StartAngle=1.74483 EndAngle=2.73189
    g3: LineSegment StartX=4.86004 StartY=25.4725 StartZ=0 EndX=7.58253 EndY=24.2107 EndZ=0
  constraints (7):
    c: Block(g0)
    c: Coincident(g1,g0)
    c: Coincident(g2,g0)
    c: Coincident(g3,g1)
    c: Coincident(g3,g2)
    c: Block(g1)
    c: Block(g2)
FEATURE [Part::Cylinder] Cylinder022
  Angle = 360
  AttacherType = Attacher::AttachEngine3D
  Height = 10
  Placement = pos=(0,0,36.15) rot=(0,0,1;0rad)
  Radius = 4
FEATURE [Sketcher::SketchObject] Sketch011  label="topSketch005"
  FullyConstrained = true
  sketch-geometry (4):
    g0: LineSegment StartX=16.8446 StartY=31.512 StartZ=0 EndX=16.3251 EndY=34.4666 EndZ=0
    g1: ArcOfCircle CenterX=19 CenterY=19.2524 CenterZ=0 NormalX=0 NormalY=0 NormalZ=1 AngleXU=0 Radius=15.4476 StartAngle=1.74483 EndAngle=2.72717
    g2: ArcOfCircle CenterX=19 CenterY=19.2524 CenterZ=0 NormalX=0 NormalY=0 NormalZ=1 AngleXU=0 Radius=12.4476 StartAngle=1.74483 EndAngle=2.73189
    g3: LineSegment StartX=4.86004 StartY=25.4725 StartZ=0 EndX=7.58253 EndY=24.2107 EndZ=0
  constraints (7):
    c: Block(g0)
    c: Coincident(g1,g0)
    c: Coincident(g2,g0)
    c: Coincident(g3,g1)
    c: Coincident(g3,g2)
    c: Block(g1)
    c: Block(g2)
FEATURE [Part::Extrusion] Extrude010
  Base = -> Sketch011
  Dir = (0,0,1)
  DirMode = 2
  FaceMakerClass = Part::FaceMakerBullseye
  LengthFwd = 10.6
  LengthRev = 0
  Placement = pos=(0,0,31) rot=(0,0,1;0rad)
  Solid = true
  Symmetric = false
FEATURE [Part::Cylinder] Cylinder023
  Angle = 360
  AttacherType = Attacher::AttachEngine3D
  Height = 20
  Placement = pos=(0,0,36.15) rot=(0,0,1;0rad)
  Radius = 8.2
FEATURE [Part::MultiFuse] Fusion039  label="removeToCreteHoleForPlugHousing008"
  Placement = pos=(-42,19,36) rot=(0,1,0;1.5708rad)
  Shapes = -> [Cylinder023,Cylinder022]
FEATURE [Part::Cut] Cut012
  Base = -> Extrude010
  Placement = pos=(0,0,-0.3) rot=(0,0,1;0rad)
  Tool = -> Fusion039
FEATURE [Part::Cut] Cut013
  Base = -> Box010
  Tool = -> Cut012
FEATURE [Part::Fillet] Fillet014
  Base = -> Cut013
  Edges = 1 edges r=0.7: [Edge13]
FEATURE [Part::Fillet] Fillet015
  Base = -> Fillet014
  Edges = 1 edges r=0.7: [Edge13]
FEATURE [Part::Fillet] Fillet016
  Base = -> Fillet015
  Edges = 1 edges r=0.7: [Edge16]
FEATURE [Part::Fillet] Fillet017
  Base = -> Fillet016
  Edges = 1 edges r=0.7: [Edge11]
FEATURE [Part::Fillet] Fillet018
  Base = -> Fillet017
  Edges = 1 edges r=0.7: [Edge10]
FEATURE [Part::Fillet] Fillet019
  Base = -> Fillet018
  Edges = 1 edges r=1.2: [Edge5]
FEATURE [Part::Fillet] Fillet020
  Base = -> Fillet019
  Edges = 1 edges r=1.2: [Edge12]
FEATURE [Part::Fillet] Fillet021
  Base = -> Fillet020
  Edges = 1 edges r=2: [Edge1]
  Placement = pos=(0.3,0,0) rot=(0,0,1;0rad)
FEATURE [Part::MultiFuse] Fusion040  label="top005"
  Shapes = -> [Cut008,Fillet021]
FEATURE [Part::MultiFuse] Fusion041  label="wireHolder"
  Shapes = -> [Fusion033,Fillet013]
FEATURE [Part::MultiFuse] Fusion042
  Shapes = -> [Fillet007,Fusion041]
FEATURE [Part::MultiFuse] Fusion043  label="wireHolder001"
  Shapes = -> [Fusion042,Fillet010]
FEATURE [Part::MultiFuse] Fusion044  label="wireHolder002"
  Shapes = -> [Fillet006,Fusion037,Fusion043]
FEATURE [Part::Feature] Face026
  shape: bbox 11 x 6 x 2e-07 mm, 1 faces, 0 solids (baked)
FEATURE [Part::Revolution] Revolve026
  Angle = 360
  Axis = (0,1,0)
  Base = (0,0,0)
  FaceMakerClass = Part::FaceMakerBullseye
  Placement = pos=(30.3,-1,19.7) rot=(0,0,1;0rad)
  Solid = false
  Source = -> Face026
  Symmetric = false
FEATURE [Sketcher::SketchObject] Sketch013  label="topSketch006"
  FullyConstrained = true
  sketch-geometry (13):
    g0: LineSegment StartX=117 StartY=19 StartZ=0 EndX=117 EndY=38 EndZ=0
    g1: ArcOfCircle CenterX=98 CenterY=19 CenterZ=0 NormalX=0 NormalY=0 NormalZ=1 AngleXU=0 Radius=19 StartAngle=5.7297 EndAngle=6.28319
    g2: LineSegment StartX=0 StartY=3 StartZ=0 EndX=0 EndY=19 EndZ=0
    g3: LineSegment StartX=19 StartY=38 StartZ=0 EndX=117 EndY=38 EndZ=0
    g4: ArcOfCircle CenterX=19 CenterY=19 CenterZ=0 NormalX=0 NormalY=0 NormalZ=1 AngleXU=0 Radius=19 StartAngle=1.5708 EndAngle=3.14159
    g5: ArcOfCircle CenterX=19 CenterY=19 CenterZ=0 NormalX=0 NormalY=0 NormalZ=1 AngleXU=0 Radius=16 StartAngle=1.5708 EndAngle=3.14159
    g6: ArcOfCircle CenterX=98 CenterY=19 CenterZ=0 NormalX=0 NormalY=0 NormalZ=1 AngleXU=0 Radius=16 StartAngle=5.60905 EndAngle=6.28319
    g7: LineSegment StartX=114 StartY=19 StartZ=0 EndX=114 EndY=35 EndZ=0
    g8: LineSegment StartX=110.5 StartY=9.01251 StartZ=0 EndX=114.163 EndY=9.01251 EndZ=0
    g9: LineSegment StartX=114 StartY=35 StartZ=0 EndX=19 EndY=35 EndZ=0
    g10: LineSegment StartX=0 StartY=3 StartZ=0 EndX=0 EndY=0 EndZ=0
    g11: LineSegment StartX=3 StartY=0 StartZ=0 EndX=0 EndY=0 EndZ=0
    g12: LineSegment StartX=3 StartY=19 StartZ=0 EndX=3 EndY=0 EndZ=0
  constraints (33):
    c: Vertical(g0)
    c: Distance(g0) = 19
    c: Block(g0)
    c: Coincident(g1,g0)
    c: Block(g1)
    c: Vertical(g2)
    c: Block(g2)
    c: Coincident(g3,g0)
    c: Horizontal(g3)
    c: Distance(g3) = 98
    c: Coincident(g4,g3)
    c: Coincident(g4,g2)
    c: Block(g4)
    c: Coincident(g5,g4)
    c: Coincident(g6,g1)
    c: Block(g6)
    c: Block(g5)
    c: Coincident(g7,g6)
    c: Vertical(g7)
    c: Coincident(g8,g6)
    c: Coincident(g8,g1)
    c: Coincident(g9,g7)
    c: Coincident(g9,g5)
    c: Horizontal(g9)
    c: Tangent(g9,g5)
    c: Coincident(g10,g2)
    c: Distance(g10) = 3
    c: Vertical(g10)
    c: Coincident(g11,g10)
    c: Horizontal(g11)
    c: Coincident(g12,g5)
    c: Coincident(g12,g11)
    c: Vertical(g12)
FEATURE [Part::Extrusion] Extrude011  label="top006"
  Base = -> Sketch013
  Dir = (0,0,1)
  DirMode = 2
  FaceMakerClass = Part::FaceMakerBullseye
  LengthFwd = 72
  LengthRev = 0
  Solid = true
  Symmetric = false
FEATURE [Sketcher::SketchObject] Sketch014
  FullyConstrained = true
  MapMode = 3
  Placement = pos=(0,0,0) rot=(1,0,0;1.5708rad)
  Support = -> [Extrude011]
  sketch-geometry (8):
    g0: Circle CenterX=80.351 CenterY=-67.6202 CenterZ=0 NormalX=0 NormalY=0 NormalZ=1 AngleXU=0 Radius=2
    g1: Circle CenterX=80.351 CenterY=-67.6202 CenterZ=0 NormalX=0 NormalY=0 NormalZ=1 AngleXU=0 Radius=3
    g2: Circle CenterX=80.351 CenterY=-4.92017 CenterZ=0 NormalX=0 NormalY=0 NormalZ=1 AngleXU=0 Radius=2
    g3: Circle CenterX=80.351 CenterY=-4.92017 CenterZ=0 NormalX=0 NormalY=0 NormalZ=1 AngleXU=0 Radius=3
    g4: Circle CenterX=23.851 CenterY=-4.92017 CenterZ=0 NormalX=0 NormalY=0 NormalZ=1 AngleXU=0 Radius=2
    g5: Circle CenterX=23.851 CenterY=-4.92017 CenterZ=0 NormalX=0 NormalY=0 NormalZ=1 AngleXU=0 Radius=3
    g6: Circle CenterX=23.851 CenterY=-67.6202 CenterZ=0 NormalX=0 NormalY=0 NormalZ=1 AngleXU=0 Radius=2
    g7: Circle CenterX=23.851 CenterY=-67.6202 CenterZ=0 NormalX=0 NormalY=0 NormalZ=1 AngleXU=0 Radius=3
  constraints (8):
    c: Block(g3)
    c: Block(g2)
    c: Block(g1)
    c: Block(g0)
    c: Block(g6)
    c: Block(g7)
    c: Block(g4)
    c: Block(g5)
FEATURE [Part::Feature] Face027
  shape: bbox 11 x 6 x 2e-07 mm, 1 faces, 0 solids (baked)
FEATURE [Part::Revolution] Revolve027
  Angle = 360
  Axis = (0,1,0)
  Base = (0,0,0)
  FaceMakerClass = Part::FaceMakerBullseye
  Placement = pos=(30.3,-1,51.7) rot=(0,0,1;0rad)
  Solid = false
  Source = -> Face027
  Symmetric = false
FEATURE [Part::Feature] Face028
  shape: bbox 11 x 6 x 2e-07 mm, 1 faces, 0 solids (baked)
FEATURE [Part::Revolution] Revolve028
  Angle = 360
  Axis = (0,1,0)
  Base = (0,0,0)
  FaceMakerClass = Part::FaceMakerBullseye
  Placement = pos=(62.3,-1,19.7) rot=(0,0,1;0rad)
  Solid = false
  Source = -> Face028
  Symmetric = false
FEATURE [Part::Feature] Face029
  shape: bbox 11 x 6 x 2e-07 mm, 1 faces, 0 solids (baked)
FEATURE [Part::Revolution] Revolve029
  Angle = 360
  Axis = (0,1,0)
  Base = (0,0,0)
  FaceMakerClass = Part::FaceMakerBullseye
  Placement = pos=(62.3,-1,51.7) rot=(0,0,1;0rad)
  Solid = false
  Source = -> Face029
  Symmetric = false
FEATURE [Part::Feature] Wire
  shape: bbox 11 x 5.2 x 2e-07 mm, 0 faces, 0 solids (baked)
FEATURE [Part::Revolution] Revolve030
  Angle = 360
  Axis = (0,1,0)
  Base = (0,0,0)
  FaceMakerClass = Part::FaceMakerBullseye
  Placement = pos=(30.3,38,19.7) rot=(0,0,1;0rad)
  Solid = true
  Source = -> Wire
  Symmetric = false
FEATURE [Part::Feature] Wire001
  shape: bbox 11 x 5.2 x 2e-07 mm, 0 faces, 0 solids (baked)
FEATURE [Part::Revolution] Revolve031
  Angle = 360
  Axis = (0,1,0)
  Base = (0,0,0)
  FaceMakerClass = Part::FaceMakerBullseye
  Placement = pos=(30.3,38,51.7) rot=(0,0,1;0rad)
  Solid = true
  Source = -> Wire001
  Symmetric = false
FEATURE [Part::Feature] Wire002
  shape: bbox 11 x 5.2 x 2e-07 mm, 0 faces, 0 solids (baked)
FEATURE [Part::Revolution] Revolve032
  Angle = 360
  Axis = (0,1,0)
  Base = (0,0,0)
  FaceMakerClass = Part::FaceMakerBullseye
  Placement = pos=(62.3,38,51.7) rot=(0,0,1;0rad)
  Solid = true
  Source = -> Wire002
  Symmetric = false
FEATURE [Part::Feature] Wire003
  shape: bbox 11 x 5.2 x 2e-07 mm, 0 faces, 0 solids (baked)
FEATURE [Part::Revolution] Revolve033
  Angle = 360
  Axis = (0,1,0)
  Base = (0,0,0)
  FaceMakerClass = Part::FaceMakerBullseye
  Placement = pos=(62.3,38,19.7) rot=(0,0,1;0rad)
  Solid = true
  Source = -> Wire003
  Symmetric = false
FEATURE [Part::MultiFuse] Fusion045  label="altRandScrewHousing"
  Shapes = -> [Revolve029,Revolve027,Revolve028,Revolve026]
FEATURE [Part::MultiFuse] Fusion046  label="fanScrewHousing"
  Shapes = -> [Revolve033,Revolve032,Revolve031,Revolve030]
FEATURE [Sketcher::SketchObject] Sketch015
  FullyConstrained = true
  sketch-geometry (17):
    g0: Circle CenterX=-3.5 CenterY=23.5 CenterZ=0 NormalX=0 NormalY=0 NormalZ=1 AngleXU=0 Radius=1
    g1: Circle CenterX=-1 CenterY=15.25 CenterZ=0 NormalX=0 NormalY=0 NormalZ=1 AngleXU=0 Radius=1
    g2: Circle CenterX=-3.5 CenterY=7 CenterZ=0 NormalX=0 NormalY=0 NormalZ=1 AngleXU=0 Radius=1
    g3: BSplineCurve PolesCount=3 KnotsCount=2 Degree=2 IsPeriodic=0
    g4: GeomPoint X=-3.5 Y=23.5 Z=0
    g5: GeomPoint X=-3.5 Y=7 Z=0
    g6: Circle CenterX=-4.8 CenterY=30.5 CenterZ=0 NormalX=0 NormalY=0 NormalZ=1 AngleXU=0 Radius=1
    g7: Circle CenterX=-3.5 CenterY=30.5 CenterZ=0 NormalX=0 NormalY=0 NormalZ=1 AngleXU=0 Radius=1
    g8: Circle CenterX=-3.5 CenterY=29.2 CenterZ=0 NormalX=0 NormalY=0 NormalZ=1 AngleXU=0 Radius=1
    g9: BSplineCurve PolesCount=3 KnotsCount=2 Degree=2 IsPeriodic=0
    g10: GeomPoint X=-4.8 Y=30.5 Z=0
    g11: GeomPoint X=-3.5 Y=29.2 Z=0
    g12: LineSegment StartX=-3.5 StartY=29.2 StartZ=0 EndX=-3.5 EndY=23.5 EndZ=0
    g13: LineSegment StartX=-4.8 StartY=30.5 StartZ=0 EndX=0 EndY=30.5 EndZ=0
    g14: LineSegment StartX=-3.5 StartY=0.3 StartZ=0 EndX=0 EndY=0.3 EndZ=0
    g15: LineSegment StartX=-3.5 StartY=0.3 StartZ=0 EndX=-3.5 EndY=7 EndZ=0
    g16: LineSegment StartX=0 StartY=0.3 StartZ=0 EndX=0 EndY=30.5 EndZ=0
  constraints (33):
    c: Weight(g0) = 1
    c: Equal(g0,g1)
    c: Equal(g0,g2)
    c: InternalAlignment(g0,g3)
    c: InternalAlignment(g1,g3)
    c: InternalAlignment(g2,g3)
    c: InternalAlignment(g4,g3)
    c: InternalAlignment(g5,g3)
    c: Block(g3)
    c: Weight(g6) = 1
    c: Equal(g6,g7)
    c: Equal(g6,g8)
    c: InternalAlignment(g6,g9)
    c: InternalAlignment(g7,g9)
    c: InternalAlignment(g8,g9)
    c: InternalAlignment(g10,g9)
    c: InternalAlignment(g11,g9)
    c: Block(g9)
    c: Coincident(g12,g9)
    c: Coincident(g12,g3)
    c: Vertical(g12)
    c: Coincident(g13,g9)
    c: Horizontal(g13)
    c: Distance(g13) = 4.8
    c: Horizontal(g14)
    c: Block(g14)
    c: Coincident(g15,g14)
    c: Coincident(g15,g3)
    c: Vertical(g15)
    c: Coincident(g16,g14)
    c: Coincident(g16,g13)
    c: Vertical(g16)
    c: Tangent(g16,g1)
FEATURE [Sketcher::SketchObject] Sketch016
  FullyConstrained = true
  sketch-geometry (16):
    g0: Circle CenterX=-3.5 CenterY=23.5 CenterZ=0 NormalX=0 NormalY=0 NormalZ=1 AngleXU=0 Radius=1
    g1: Circle CenterX=-1 CenterY=15.25 CenterZ=0 NormalX=0 NormalY=0 NormalZ=1 AngleXU=0 Radius=1
    g2: Circle CenterX=-3.5 CenterY=7 CenterZ=0 NormalX=0 NormalY=0 NormalZ=1 AngleXU=0 Radius=1
    g3: BSplineCurve PolesCount=3 KnotsCount=2 Degree=2 IsPeriodic=0
    g4: GeomPoint X=-3.5 Y=23.5 Z=0
    g5: GeomPoint X=-3.5 Y=7 Z=0
    g6: LineSegment StartX=-3.5 StartY=28.2 StartZ=0 EndX=-3.5 EndY=23.5 EndZ=0
    g7: LineSegment StartX=0 StartY=29.5 StartZ=0 EndX=0 EndY=30 EndZ=0
    g8: LineSegment StartX=-3.5 StartY=28.2 StartZ=0 EndX=-3.5 EndY=30 EndZ=0
    g9: LineSegment StartX=0 StartY=30 StartZ=0 EndX=0 EndY=30.5 EndZ=0
    g10: LineSegment StartX=0 StartY=30.5 StartZ=0 EndX=-3.5 EndY=30.5 EndZ=0
    g11: LineSegment StartX=-3.5 StartY=30.5 StartZ=0 EndX=-3.5 EndY=30 EndZ=0
    g12: LineSegment StartX=0 StartY=29.5 StartZ=0 EndX=0 EndY=5 EndZ=0
    g13: LineSegment StartX=-3.5 StartY=0.3 StartZ=0 EndX=-3.5 EndY=7 EndZ=0
    g14: LineSegment StartX=-3.5 StartY=0.3 StartZ=0 EndX=0 EndY=0.3 EndZ=0
    g15: LineSegment StartX=0 StartY=5 StartZ=0 EndX=0 EndY=0.3 EndZ=0
  constraints (39):
    c: Weight(g0) = 1
    c: Equal(g0,g1)
    c: Equal(g0,g2)
    c: InternalAlignment(g0,g3)
    c: InternalAlignment(g1,g3)
    c: InternalAlignment(g2,g3)
    c: InternalAlignment(g4,g3)
    c: InternalAlignment(g5,g3)
    c: Block(g3)
    c: Coincident(g6,g3)
    c: Vertical(g6)
    c: Vertical(g7)
    c: Distance(g7) = 0.5
    c: Coincident(g8,g6)
    c: Vertical(g8)
    c: Block(g6)
    c: Block(g7)
    c: Vertical(g9)
    c: Equal(g7,g9) = 0.5
    c: Block(g9)
    c: Coincident(g9,g7)
    c: Horizontal(g10)
    c: Coincident(g10,g9)
    c: Coincident(g11,g10)
    c: Coincident(g11,g8)
    c: Vertical(g11)
    c: Block(g11)
    c: Coincident(g12,g7)
    c: Vertical(g12)
    c: Coincident(g13,g3)
    c: Vertical(g13)
    c: Distance(g13) = 6.7
    c: Coincident(g14,g13)
    c: Horizontal(g14)
    c: Block(g14)
    c: Coincident(g15,g12)
    c: Coincident(g15,g14)
    c: Vertical(g15)
    c: Block(g15)
FEATURE [Sketcher::SketchObject] Sketch017
  FullyConstrained = true
  sketch-geometry (11):
    g0: LineSegment StartX=-3.5 StartY=1e-16 StartZ=0 EndX=-1.6 EndY=1e-16 EndZ=0
    g1: LineSegment StartX=-1.6 StartY=1e-16 StartZ=0 EndX=-1.6 EndY=1.5 EndZ=0
    g2: LineSegment StartX=-3.5 StartY=1.5 StartZ=0 EndX=-1.6 EndY=1.5 EndZ=0
    g3: LineSegment StartX=-3.5 StartY=1e-16 StartZ=0 EndX=-4.8 EndY=1e-16 EndZ=0
    g4: Circle CenterX=-3.5 CenterY=1.3 CenterZ=0 NormalX=0 NormalY=0 NormalZ=1 AngleXU=0 Radius=1
    g5: Circle CenterX=-3.5 CenterY=1e-16 CenterZ=0 NormalX=0 NormalY=0 NormalZ=1 AngleXU=0 Radius=1
    g6: Circle CenterX=-4.8 CenterY=1e-16 CenterZ=0 NormalX=0 NormalY=0 NormalZ=1 AngleXU=0 Radius=1
    g7: BSplineCurve PolesCount=3 KnotsCount=2 Degree=2 IsPeriodic=0
    g8: GeomPoint X=-3.5 Y=1.3 Z=0
    g9: GeomPoint X=-4.8 Y=1e-16 Z=0
    g10: LineSegment StartX=-3.5 StartY=1.3 StartZ=0 EndX=-3.5 EndY=1.5 EndZ=0
  constraints (24):
    c: Horizontal(g0)
    c: Distance(g0) = 1.9
    c: Block(g0)
    c: Coincident(g1,g0)
    c: Vertical(g1)
    c: Coincident(g2,g1)
    c: Horizontal(g2)
    c: Coincident(g3,g0)
    c: Horizontal(g3)
    c: Distance(g3) = 1.3
    c: Weight(g4) = 1
    c: Equal(g4,g5)
    c: Coincident(g5,g0)
    c: Equal(g4,g6)
    c: Coincident(g7,g3)
    c: InternalAlignment(g4,g7)
    c: InternalAlignment(g5,g7)
    c: InternalAlignment(g6,g7)
    c: InternalAlignment(g8,g7)
    c: InternalAlignment(g9,g7)
    c: Coincident(g10,g7)
    c: Coincident(g10,g2)
    c: Vertical(g10)
    c: Block(g10)
FEATURE [Part::Feature] Face035
  shape: bbox 3.2 x 1.5 x 2e-07 mm, 1 faces, 0 solids (baked)
FEATURE [Part::Revolution] Revolve039  label="backCaseScrewRetainer"
  Angle = 360
  Axis = (0,1,0)
  Base = (0,0,0)
  FaceMakerClass = Part::FaceMakerBullseye
  Placement = pos=(12.5,3,62) rot=(0,0,1;0rad)
  Solid = false
  Source = -> Face035
  Symmetric = false
FEATURE [Part::Feature] Face036
  shape: bbox 3.2 x 1.5 x 2e-07 mm, 1 faces, 0 solids (baked)
FEATURE [Part::Feature] Face039
  shape: bbox 4.8 x 30.2 x 2e-07 mm, 1 faces, 0 solids (baked)
FEATURE [Part::Revolution] Revolve043  label="frontCaseScrewPost002"
  Angle = 360
  Axis = (0,1,0)
  Base = (0,0,0)
  FaceMakerClass = Part::FaceMakerBullseye
  Placement = pos=(89.5,4.5,3.5) rot=(0,0,1;0rad)
  Solid = false
  Source = -> Face039
  Symmetric = false
FEATURE [Part::Feature] Face042
  shape: bbox 4.8 x 30.2 x 2e-07 mm, 1 faces, 0 solids (baked)
FEATURE [Part::Revolution] Revolve046  label="frontCaseScrewPost003"
  Angle = 360
  Axis = (0,1,0)
  Base = (0,0,0)
  FaceMakerClass = Part::FaceMakerBullseye
  Placement = pos=(89.5,4.5,68.5) rot=(0,0,1;0rad)
  Solid = false
  Source = -> Face042
  Symmetric = false
FEATURE [Part::Feature] Face043
  shape: bbox 3.2 x 1.5 x 2e-07 mm, 1 faces, 0 solids (baked)
FEATURE [Part::Revolution] Revolve047  label="frontCaseScrewRetainer002"
  Angle = 360
  Axis = (0,1,0)
  Base = (0,0,0)
  FaceMakerClass = Part::FaceMakerBullseye
  Placement = pos=(89.5,3,68.5) rot=(0,0,1;0rad)
  Solid = false
  Source = -> Face043
  Symmetric = false
FEATURE [Part::Feature] Face044
  shape: bbox 3.2 x 1.5 x 2e-07 mm, 1 faces, 0 solids (baked)
FEATURE [Part::Revolution] Revolve048  label="frontCaseScrewRetainer003"
  Angle = 360
  Axis = (0,1,0)
  Base = (0,0,0)
  FaceMakerClass = Part::FaceMakerBullseye
  Placement = pos=(89.5,3,3.5) rot=(0,0,1;0rad)
  Solid = false
  Source = -> Face044
  Symmetric = false
FEATURE [App::MeasureDistance] Distance002  label="Distance: 1.67 mm"
  Distance = 1.66921
  P1 = (99.2361,4.7524,71.7)
  P2 = (99.2347,6.42161,71.7)
FEATURE [Sketcher::SketchObject] Sketch018
  FullyConstrained = true
  sketch-geometry (7):
    g0: LineSegment StartX=0 StartY=0 StartZ=0 EndX=0 EndY=6 EndZ=0
    g1: Circle CenterX=0 CenterY=0 CenterZ=0 NormalX=0 NormalY=0 NormalZ=1 AngleXU=0 Radius=1
    g2: Circle CenterX=8 CenterY=6 CenterZ=0 NormalX=0 NormalY=0 NormalZ=1 AngleXU=0 Radius=1
    g3: BSplineCurve PolesCount=3 KnotsCount=2 Degree=2 IsPeriodic=0
    g4: GeomPoint X=0 Y=0 Z=0
    g5: GeomPoint X=8 Y=6 Z=0
    g6: LineSegment StartX=0 StartY=6 StartZ=0 EndX=8 EndY=6 EndZ=0
  constraints (14):
    c: Coincident(g0,g-1)
    c: Distance(g0) = 6
    c: Vertical(g0)
    c: Coincident(g3,g0)
    c: Weight(g1) = 1
    c: Equal(g1,g2)
    c: InternalAlignment(g1,g3)
    c: InternalAlignment(g2,g3)
    c: InternalAlignment(g4,g3)
    c: InternalAlignment(g5,g3)
    c: Block(g3)
    c: Coincident(g6,g0)
    c: Coincident(g6,g3)
    c: Horizontal(g6)
FEATURE [Part::Extrusion] Extrude012  label="caseScrewPillarBracket"
  Base = -> Sketch018
  Dir = (0,0,1)
  DirMode = 2
  FaceMakerClass = Part::FaceMakerBullseye
  LengthFwd = 2.4
  LengthRev = 0
  Placement = pos=(15.76,29,8.8) rot=(0,1,0;0rad)
  Solid = true
  Symmetric = false
FEATURE [Sketcher::SketchObject] Sketch019
  FullyConstrained = true
  sketch-geometry (7):
    g0: LineSegment StartX=0 StartY=0 StartZ=0 EndX=0 EndY=6 EndZ=0
    g1: Circle CenterX=0 CenterY=0 CenterZ=0 NormalX=0 NormalY=0 NormalZ=1 AngleXU=0 Radius=1
    g2: Circle CenterX=8 CenterY=6 CenterZ=0 NormalX=0 NormalY=0 NormalZ=1 AngleXU=0 Radius=1
    g3: BSplineCurve PolesCount=3 KnotsCount=2 Degree=2 IsPeriodic=0
    g4: GeomPoint X=0 Y=0 Z=0
    g5: GeomPoint X=8 Y=6 Z=0
    g6: LineSegment StartX=0 StartY=6 StartZ=0 EndX=8 EndY=6 EndZ=0
  constraints (14):
    c: Coincident(g0,g-1)
    c: Distance(g0) = 6
    c: Vertical(g0)
    c: Coincident(g3,g0)
    c: Weight(g1) = 1
    c: Equal(g1,g2)
    c: InternalAlignment(g1,g3)
    c: InternalAlignment(g2,g3)
    c: InternalAlignment(g4,g3)
    c: InternalAlignment(g5,g3)
    c: Block(g3)
    c: Coincident(g6,g0)
    c: Coincident(g6,g3)
    c: Horizontal(g6)
FEATURE [Part::Extrusion] Extrude013  label="caseScrewPillarBracket001"
  Base = -> Sketch019
  Dir = (0,0,1)
  DirMode = 2
  FaceMakerClass = Part::FaceMakerBullseye
  LengthFwd = 2.4
  LengthRev = 0
  Placement = pos=(15.76,29,60.8) rot=(0,0,1;0rad)
  Solid = true
  Symmetric = false
FEATURE [Sketcher::SketchObject] Sketch020
  FullyConstrained = true
  sketch-geometry (7):
    g0: LineSegment StartX=0 StartY=0 StartZ=0 EndX=0 EndY=6 EndZ=0
    g1: Circle CenterX=0 CenterY=0 CenterZ=0 NormalX=0 NormalY=0 NormalZ=1 AngleXU=0 Radius=1
    g2: Circle CenterX=8 CenterY=6 CenterZ=0 NormalX=0 NormalY=0 NormalZ=1 AngleXU=0 Radius=1
    g3: BSplineCurve PolesCount=3 KnotsCount=2 Degree=2 IsPeriodic=0
    g4: GeomPoint X=0 Y=0 Z=0
    g5: GeomPoint X=8 Y=6 Z=0
    g6: LineSegment StartX=0 StartY=6 StartZ=0 EndX=8 EndY=6 EndZ=0
  constraints (14):
    c: Coincident(g0,g-1)
    c: Distance(g0) = 6
    c: Vertical(g0)
    c: Coincident(g3,g0)
    c: Weight(g1) = 1
    c: Equal(g1,g2)
    c: InternalAlignment(g1,g3)
    c: InternalAlignment(g2,g3)
    c: InternalAlignment(g4,g3)
    c: InternalAlignment(g5,g3)
    c: Block(g3)
    c: Coincident(g6,g0)
    c: Coincident(g6,g3)
    c: Horizontal(g6)
FEATURE [Part::Extrusion] Extrude014  label="caseScrewPillarBracket002"
  Base = -> Sketch020
  Dir = (0,0,1)
  DirMode = 2
  FaceMakerClass = Part::FaceMakerBullseye
  LengthFwd = 2.4
  LengthRev = 0
  Placement = pos=(13.7,29,13.26) rot=(0,1,0;-1.5708rad)
  Solid = true
  Symmetric = false
FEATURE [Sketcher::SketchObject] Sketch021
  FullyConstrained = true
  sketch-geometry (7):
    g0: LineSegment StartX=0 StartY=0 StartZ=0 EndX=0 EndY=6 EndZ=0
    g1: Circle CenterX=0 CenterY=0 CenterZ=0 NormalX=0 NormalY=0 NormalZ=1 AngleXU=0 Radius=1
    g2: Circle CenterX=8 CenterY=6 CenterZ=0 NormalX=0 NormalY=0 NormalZ=1 AngleXU=0 Radius=1
    g3: BSplineCurve PolesCount=3 KnotsCount=2 Degree=2 IsPeriodic=0
    g4: GeomPoint X=0 Y=0 Z=0
    g5: GeomPoint X=8 Y=6 Z=0
    g6: LineSegment StartX=0 StartY=6 StartZ=0 EndX=8 EndY=6 EndZ=0
  constraints (14):
    c: Coincident(g0,g-1)
    c: Distance(g0) = 6
    c: Vertical(g0)
    c: Coincident(g3,g0)
    c: Weight(g1) = 1
    c: Equal(g1,g2)
    c: InternalAlignment(g1,g3)
    c: InternalAlignment(g2,g3)
    c: InternalAlignment(g4,g3)
    c: InternalAlignment(g5,g3)
    c: Block(g3)
    c: Coincident(g6,g0)
    c: Coincident(g6,g3)
    c: Horizontal(g6)
FEATURE [Part::Extrusion] Extrude015  label="caseScrewPillarBracket003"
  Base = -> Sketch021
  Dir = (0,0,1)
  DirMode = 2
  FaceMakerClass = Part::FaceMakerBullseye
  LengthFwd = 2.4
  LengthRev = 0
  Placement = pos=(11.3,29,58.74) rot=(0,1,0;1.5708rad)
  Solid = true
  Symmetric = false
FEATURE [Sketcher::SketchObject] Sketch022
  FullyConstrained = true
  sketch-geometry (7):
    g0: LineSegment StartX=0 StartY=0 StartZ=0 EndX=0 EndY=6 EndZ=0
    g1: Circle CenterX=0 CenterY=0 CenterZ=0 NormalX=0 NormalY=0 NormalZ=1 AngleXU=0 Radius=1
    g2: Circle CenterX=8 CenterY=6 CenterZ=0 NormalX=0 NormalY=0 NormalZ=1 AngleXU=0 Radius=1
    g3: BSplineCurve PolesCount=3 KnotsCount=2 Degree=2 IsPeriodic=0
    g4: GeomPoint X=0 Y=0 Z=0
    g5: GeomPoint X=8 Y=6 Z=0
    g6: LineSegment StartX=0 StartY=6 StartZ=0 EndX=8 EndY=6 EndZ=0
  constraints (14):
    c: Coincident(g0,g-1)
    c: Distance(g0) = 6
    c: Vertical(g0)
    c: Coincident(g3,g0)
    c: Weight(g1) = 1
    c: Equal(g1,g2)
    c: InternalAlignment(g1,g3)
    c: InternalAlignment(g2,g3)
    c: InternalAlignment(g4,g3)
    c: InternalAlignment(g5,g3)
    c: Block(g3)
    c: Coincident(g6,g0)
    c: Coincident(g6,g3)
    c: Horizontal(g6)
FEATURE [Part::Extrusion] Extrude016  label="caseScrewPillarBracket004"
  Base = -> Sketch022
  Dir = (0,0,1)
  DirMode = 2
  FaceMakerClass = Part::FaceMakerBullseye
  LengthFwd = 2.4
  LengthRev = 0
  Placement = pos=(88.3,29,65.23) rot=(0,1,0;1.5708rad)
  Solid = true
  Symmetric = false
FEATURE [Sketcher::SketchObject] Sketch023
  FullyConstrained = true
  sketch-geometry (7):
    g0: LineSegment StartX=0 StartY=0 StartZ=0 EndX=0 EndY=6 EndZ=0
    g1: Circle CenterX=0 CenterY=0 CenterZ=0 NormalX=0 NormalY=0 NormalZ=1 AngleXU=0 Radius=1
    g2: Circle CenterX=8 CenterY=6 CenterZ=0 NormalX=0 NormalY=0 NormalZ=1 AngleXU=0 Radius=1
    g3: BSplineCurve PolesCount=3 KnotsCount=2 Degree=2 IsPeriodic=0
    g4: GeomPoint X=0 Y=0 Z=0
    g5: GeomPoint X=8 Y=6 Z=0
    g6: LineSegment StartX=0 StartY=6 StartZ=0 EndX=8 EndY=6 EndZ=0
  constraints (14):
    c: Coincident(g0,g-1)
    c: Distance(g0) = 6
    c: Vertical(g0)
    c: Coincident(g3,g0)
    c: Weight(g1) = 1
    c: Equal(g1,g2)
    c: InternalAlignment(g1,g3)
    c: InternalAlignment(g2,g3)
    c: InternalAlignment(g4,g3)
    c: InternalAlignment(g5,g3)
    c: Block(g3)
    c: Coincident(g6,g0)
    c: Coincident(g6,g3)
    c: Horizontal(g6)
FEATURE [Part::Extrusion] Extrude017  label="caseScrewPillarBracket005"
  Base = -> Sketch023
  Dir = (0,0,1)
  DirMode = 2
  FaceMakerClass = Part::FaceMakerBullseye
  LengthFwd = 2.4
  LengthRev = 0
  Placement = pos=(90.7,29,6.77) rot=(0,-1,0;1.5708rad)
  Solid = true
  Symmetric = false
FEATURE [Sketcher::SketchObject] Sketch024
  FullyConstrained = true
  sketch-geometry (7):
    g0: LineSegment StartX=0 StartY=0 StartZ=0 EndX=0 EndY=6 EndZ=0
    g1: Circle CenterX=0 CenterY=0 CenterZ=0 NormalX=0 NormalY=0 NormalZ=1 AngleXU=0 Radius=1
    g2: Circle CenterX=8 CenterY=6 CenterZ=0 NormalX=0 NormalY=0 NormalZ=1 AngleXU=0 Radius=1
    g3: BSplineCurve PolesCount=3 KnotsCount=2 Degree=2 IsPeriodic=0
    g4: GeomPoint X=0 Y=0 Z=0
    g5: GeomPoint X=8 Y=6 Z=0
    g6: LineSegment StartX=0 StartY=6 StartZ=0 EndX=8 EndY=6 EndZ=0
  constraints (14):
    c: Coincident(g0,g-1)
    c: Distance(g0) = 6
    c: Vertical(g0)
    c: Coincident(g3,g0)
    c: Weight(g1) = 1
    c: Equal(g1,g2)
    c: InternalAlignment(g1,g3)
    c: InternalAlignment(g2,g3)
    c: InternalAlignment(g4,g3)
    c: InternalAlignment(g5,g3)
    c: Block(g3)
    c: Coincident(g6,g0)
    c: Coincident(g6,g3)
    c: Horizontal(g6)
FEATURE [Part::Extrusion] Extrude018  label="caseScrewPillarBracket006"
  Base = -> Sketch024
  Dir = (0,0,1)
  DirMode = 2
  FaceMakerClass = Part::FaceMakerBullseye
  LengthFwd = 2.4
  LengthRev = 0
  Placement = pos=(103.7,29,6.77) rot=(0,-1,0;1.5708rad)
  Solid = true
  Symmetric = false
FEATURE [Sketcher::SketchObject] Sketch025
  FullyConstrained = true
  sketch-geometry (7):
    g0: LineSegment StartX=0 StartY=0 StartZ=0 EndX=0 EndY=6 EndZ=0
    g1: Circle CenterX=0 CenterY=0 CenterZ=0 NormalX=0 NormalY=0 NormalZ=1 AngleXU=0 Radius=1
    g2: Circle CenterX=8 CenterY=6 CenterZ=0 NormalX=0 NormalY=0 NormalZ=1 AngleXU=0 Radius=1
    g3: BSplineCurve PolesCount=3 KnotsCount=2 Degree=2 IsPeriodic=0
    g4: GeomPoint X=0 Y=0 Z=0
    g5: GeomPoint X=8 Y=6 Z=0
    g6: LineSegment StartX=0 StartY=6 StartZ=0 EndX=8 EndY=6 EndZ=0
  constraints (14):
    c: Coincident(g0,g-1)
    c: Distance(g0) = 6
    c: Vertical(g0)
    c: Coincident(g3,g0)
    c: Weight(g1) = 1
    c: Equal(g1,g2)
    c: InternalAlignment(g1,g3)
    c: InternalAlignment(g2,g3)
    c: InternalAlignment(g4,g3)
    c: InternalAlignment(g5,g3)
    c: Block(g3)
    c: Coincident(g6,g0)
    c: Coincident(g6,g3)
    c: Horizontal(g6)
FEATURE [Part::Extrusion] Extrude019  label="caseScrewPillarBracket007"
  Base = -> Sketch025
  Dir = (0,0,1)
  DirMode = 2
  FaceMakerClass = Part::FaceMakerBullseye
  LengthFwd = 2.4
  LengthRev = 0
  Placement = pos=(101.3,29,65.23) rot=(0,1,0;1.5708rad)
  Solid = true
  Symmetric = false
FEATURE [Part::Box] Box011  label="frontCaseScrewPillarBracket"
  AttacherType = Attacher::AttachEngine3D
  Height = 2.4
  Length = 16
  Placement = pos=(87,28,2.3) rot=(0,0,1;0rad)
  Width = 7
FEATURE [Part::Box] Box012  label="frontCaseScrewPillarBracket001"
  AttacherType = Attacher::AttachEngine3D
  Height = 2.4
  Length = 16
  Placement = pos=(87,28,67.3) rot=(0,0,1;0rad)
  Width = 7
FEATURE [Sketcher::SketchObject] Sketch026
  FullyConstrained = true
  sketch-geometry (17):
    g0: Circle CenterX=-3.5 CenterY=23.5 CenterZ=0 NormalX=0 NormalY=0 NormalZ=1 AngleXU=0 Radius=1
    g1: Circle CenterX=-1 CenterY=15.25 CenterZ=0 NormalX=0 NormalY=0 NormalZ=1 AngleXU=0 Radius=1
    g2: Circle CenterX=-3.5 CenterY=7 CenterZ=0 NormalX=0 NormalY=0 NormalZ=1 AngleXU=0 Radius=1
    g3: BSplineCurve PolesCount=3 KnotsCount=2 Degree=2 IsPeriodic=0
    g4: GeomPoint X=-3.5 Y=23.5 Z=0
    g5: GeomPoint X=-3.5 Y=7 Z=0
    g6: Circle CenterX=-4.8 CenterY=30.5 CenterZ=0 NormalX=0 NormalY=0 NormalZ=1 AngleXU=0 Radius=1
    g7: Circle CenterX=-3.5 CenterY=30.5 CenterZ=0 NormalX=0 NormalY=0 NormalZ=1 AngleXU=0 Radius=1
    g8: Circle CenterX=-3.5 CenterY=29.2 CenterZ=0 NormalX=0 NormalY=0 NormalZ=1 AngleXU=0 Radius=1
    g9: BSplineCurve PolesCount=3 KnotsCount=2 Degree=2 IsPeriodic=0
    g10: GeomPoint X=-4.8 Y=30.5 Z=0
    g11: GeomPoint X=-3.5 Y=29.2 Z=0
    g12: LineSegment StartX=-3.5 StartY=29.2 StartZ=0 EndX=-3.5 EndY=23.5 EndZ=0
    g13: LineSegment StartX=-4.8 StartY=30.5 StartZ=0 EndX=0 EndY=30.5 EndZ=0
    g14: LineSegment StartX=-3.5 StartY=5 StartZ=0 EndX=-3.5 EndY=7 EndZ=0
    g15: LineSegment StartX=0 StartY=5 StartZ=0 EndX=0 EndY=30.5 EndZ=0
    g16: LineSegment StartX=-3.5 StartY=5 StartZ=0 EndX=0 EndY=5 EndZ=0
  constraints (33):
    c: Weight(g0) = 1
    c: Equal(g0,g1)
    c: Equal(g0,g2)
    c: InternalAlignment(g0,g3)
    c: InternalAlignment(g1,g3)
    c: InternalAlignment(g2,g3)
    c: InternalAlignment(g4,g3)
    c: InternalAlignment(g5,g3)
    c: Block(g3)
    c: Weight(g6) = 1
    c: Equal(g6,g7)
    c: Equal(g6,g8)
    c: InternalAlignment(g6,g9)
    c: InternalAlignment(g7,g9)
    c: InternalAlignment(g8,g9)
    c: InternalAlignment(g10,g9)
    c: InternalAlignment(g11,g9)
    c: Block(g9)
    c: Coincident(g12,g9)
    c: Coincident(g12,g3)
    c: Vertical(g12)
    c: Coincident(g13,g9)
    c: Horizontal(g13)
    c: Distance(g13) = 4.8
    c: Coincident(g14,g3)
    c: Vertical(g14)
    c: Coincident(g15,g13)
    c: Vertical(g15)
    c: Tangent(g15,g1)
    c: Distance(g14) = 2
    c: Coincident(g16,g14)
    c: Horizontal(g16)
    c: Coincident(g15,g16)
FEATURE [Part::Feature] Face050
  shape: bbox 4.8 x 25.5 x 2e-07 mm, 1 faces, 0 solids (baked)
FEATURE [Part::Revolution] Revolve054  label="moreFrontCaseScrewPost001"
  Angle = 360
  Axis = (0,1,0)
  Base = (0,0,0)
  FaceMakerClass = Part::FaceMakerBullseye
  Placement = pos=(102.5,4.5,3.5) rot=(0,0,1;0rad)
  Solid = false
  Source = -> Face050
  Symmetric = false
FEATURE [Part::Feature] Face051
  shape: bbox 4.8 x 25.5 x 2e-07 mm, 1 faces, 0 solids (baked)
FEATURE [Part::Revolution] Revolve055  label="moreFrontCaseScrewPost002"
  Angle = 360
  Axis = (0,1,0)
  Base = (0,0,0)
  FaceMakerClass = Part::FaceMakerBullseye
  Placement = pos=(102.5,4.5,68.5) rot=(0,0,1;0rad)
  Solid = false
  Source = -> Face051
  Symmetric = false
FEATURE [Sketcher::SketchObject] Sketch027
  FullyConstrained = true
  sketch-geometry (10):
    g0: LineSegment StartX=-1.6 StartY=4.7 StartZ=0 EndX=-1.6 EndY=1.7 EndZ=0
    g1: LineSegment StartX=-3.5 StartY=4.7 StartZ=0 EndX=-1.6 EndY=4.7 EndZ=0
    g2: LineSegment StartX=-1.6 StartY=1.7 StartZ=0 EndX=-1.6 EndY=1.5 EndZ=0
    g3: LineSegment StartX=-1.6 StartY=1.5 StartZ=0 EndX=-5.2 EndY=1.5 EndZ=0
    g4: Circle CenterX=-3.5 CenterY=4.7 CenterZ=0 NormalX=0 NormalY=0 NormalZ=1 AngleXU=0 Radius=1
    g5: Circle CenterX=-3.59627 CenterY=2.99743 CenterZ=0 NormalX=0 NormalY=0 NormalZ=1 AngleXU=0 Radius=1
    g6: Circle CenterX=-5.2 CenterY=1.5 CenterZ=0 NormalX=0 NormalY=0 NormalZ=1 AngleXU=0 Radius=1
    g7: BSplineCurve PolesCount=3 KnotsCount=2 Degree=2 IsPeriodic=0
    g8: GeomPoint X=-3.5 Y=4.7 Z=0
    g9: GeomPoint X=-5.2 Y=1.5 Z=0
  constraints (23):
    c: Vertical(g0)
    c: Distance(g0) = 3
    c: Coincident(g1,g0)
    c: Horizontal(g1)
    c: Block(g0)
    c: Block(g1)
    c: Coincident(g2,g0)
    c: Vertical(g2)
    c: Distance(g2) = 0.2
    c: Coincident(g3,g2)
    c: Horizontal(g3)
    c: Block(g3)
    c: Coincident(g7,g1)
    c: Weight(g4) = 1
    c: Equal(g4,g5)
    c: Equal(g4,g6)
    c: Coincident(g7,g3)
    c: InternalAlignment(g4,g7)
    c: InternalAlignment(g5,g7)
    c: InternalAlignment(g6,g7)
    c: InternalAlignment(g8,g7)
    c: InternalAlignment(g9,g7)
    c: Block(g7)
FEATURE [Sketcher::SketchObject] Sketch028
  FullyConstrained = true
  sketch-geometry (18):
    g0: LineSegment StartX=0 StartY=3e-16 StartZ=0 EndX=0 EndY=1.7 EndZ=0
    g1: LineSegment StartX=-3.5 StartY=0 StartZ=0 EndX=-3.5 EndY=0.9 EndZ=0
    g2: Circle CenterX=-2.7 CenterY=1.7 CenterZ=0 NormalX=0 NormalY=0 NormalZ=1 AngleXU=0 Radius=1
    g3: Circle CenterX=-3.5 CenterY=1.7 CenterZ=0 NormalX=0 NormalY=0 NormalZ=1 AngleXU=0 Radius=1
    g4: Circle CenterX=-3.5 CenterY=0.9 CenterZ=0 NormalX=0 NormalY=0 NormalZ=1 AngleXU=0 Radius=1
    g5: BSplineCurve PolesCount=3 KnotsCount=2 Degree=2 IsPeriodic=0
    g6: GeomPoint X=-2.7 Y=1.7 Z=0
    g7: GeomPoint X=-3.5 Y=0.9 Z=0
    g8: LineSegment StartX=-3.5 StartY=0 StartZ=0 EndX=-3.5 EndY=-7 EndZ=0
    g9: LineSegment StartX=0 StartY=3e-16 StartZ=0 EndX=0 EndY=-7 EndZ=0
    g10: LineSegment StartX=-3.5 StartY=-7 StartZ=0 EndX=0 EndY=-7 EndZ=0
    g11: LineSegment StartX=-2.7 StartY=1.7 StartZ=0 EndX=-1.6 EndY=1.7 EndZ=0
    g12: LineSegment StartX=0 StartY=1.7 StartZ=0 EndX=0 EndY=4.5 EndZ=0
    g13: LineSegment StartX=0 StartY=4.5 StartZ=0 EndX=0 EndY=10.8 EndZ=0
    g14: LineSegment StartX=0 StartY=10.8 StartZ=0 EndX=-2 EndY=10.8 EndZ=0
    g15: LineSegment StartX=-1.6 StartY=4.7 StartZ=0 EndX=-1.6 EndY=1.7 EndZ=0
    g16: LineSegment StartX=-1.6 StartY=4.7 StartZ=0 EndX=-2 EndY=4.7 EndZ=0
    g17: LineSegment StartX=-2 StartY=4.7 StartZ=0 EndX=-2 EndY=10.8 EndZ=0
  constraints (44):
    c: Vertical(g0)
    c: Vertical(g1)
    c: Distance(g1) = 0.9
    c: Block(g0)
    c: Distance(g0) = 1.7
    c: Weight(g2) = 1
    c: Equal(g2,g3)
    c: Equal(g2,g4)
    c: Coincident(g5,g1)
    c: InternalAlignment(g2,g5)
    c: InternalAlignment(g3,g5)
    c: InternalAlignment(g4,g5)
    c: InternalAlignment(g6,g5)
    c: InternalAlignment(g7,g5)
    c: Block(g5)
    c: Coincident(g8,g1)
    c: Vertical(g8)
    c: Distance(g8) = 7
    c: Vertical(g9)
    c: Equal(g8,g9) = 7
    c: Coincident(g9,g0)
    c: Coincident(g10,g8)
    c: Coincident(g10,g9)
    c: Horizontal(g10)
    c: Coincident(g11,g5)
    c: Horizontal(g11)
    c: Coincident(g12,g0)
    c: Vertical(g12)
    c: Distance(g12) = 2.8
    c: Coincident(g13,g12)
    c: Vertical(g13)
    c: Distance(g13) = 6.3
    c: Coincident(g14,g13)
    c: Horizontal(g14)
    c: Distance(g14) = 2
    c: Vertical(g15)
    c: Distance(g15) = 3
    c: Block(g11)
    c: Coincident(g15,g11)
    c: Coincident(g16,g15)
    c: Horizontal(g16)
    c: Coincident(g17,g16)
    c: Coincident(g17,g14)
    c: Vertical(g17)
FEATURE [Part::Revolution] Revolve040  label="backCaseScrewRetainer001"
  Angle = 360
  Axis = (0,1,0)
  Base = (0,0,0)
  FaceMakerClass = Part::FaceMakerBullseye
  Placement = pos=(12.5,3,10) rot=(0,0,1;0rad)
  Solid = false
  Source = -> Face036
  Symmetric = false
FEATURE [Part::Feature] Face055
  shape: bbox 3.5 x 30.2 x 2e-07 mm, 1 faces, 0 solids (baked)
FEATURE [Part::Revolution] Revolve059  label="backCaseScrewPost"
  Angle = 360
  Axis = (0,1,0)
  Base = (0,0,0)
  FaceMakerClass = Part::FaceMakerBullseye
  Placement = pos=(12.5,4.5,10) rot=(0,0,1;0rad)
  Solid = false
  Source = -> Face055
  Symmetric = false
FEATURE [Part::Feature] Face056
  shape: bbox 3.5 x 30.2 x 2e-07 mm, 1 faces, 0 solids (baked)
FEATURE [Part::Revolution] Revolve060  label="backCaseScrewPost001"
  Angle = 360
  Axis = (0,1,0)
  Base = (0,0,0)
  FaceMakerClass = Part::FaceMakerBullseye
  Placement = pos=(12.5,4.5,62) rot=(0,0,1;0rad)
  Solid = false
  Source = -> Face056
  Symmetric = false
FEATURE [Part::Feature] Face057
  shape: bbox 3.5 x 17.8 x 2e-07 mm, 1 faces, 0 solids (baked)
FEATURE [Part::Revolution] Revolve061  label="removeToCreateScrewAndThreadedInsertHole"
  Angle = 360
  Axis = (0,1,0)
  Base = (0,0,0)
  FaceMakerClass = Part::FaceMakerBullseye
  Placement = pos=(12.5,0,10) rot=(0,0,1;0rad)
  Solid = false
  Source = -> Face057
  Symmetric = false
FEATURE [Part::Feature] Face058
  shape: bbox 3.5 x 17.8 x 2e-07 mm, 1 faces, 0 solids (baked)
FEATURE [Part::Revolution] Revolve062  label="removeToCreateScrewAndThreadedInsertHole001"
  Angle = 360
  Axis = (0,1,0)
  Base = (0,0,0)
  FaceMakerClass = Part::FaceMakerBullseye
  Placement = pos=(12.5,0,62) rot=(0,0,1;0rad)
  Solid = false
  Source = -> Face058
  Symmetric = false
FEATURE [Part::Feature] Face059
  shape: bbox 3.5 x 17.8 x 2e-07 mm, 1 faces, 0 solids (baked)
FEATURE [Part::Revolution] Revolve063  label="removeToCreateScrewAndThreadedInsertHole002"
  Angle = 360
  Axis = (0,1,0)
  Base = (0,0,0)
  FaceMakerClass = Part::FaceMakerBullseye
  Placement = pos=(89.5,0,68.5) rot=(0,0,1;0rad)
  Solid = false
  Source = -> Face059
  Symmetric = false
FEATURE [Part::Feature] Face060
  shape: bbox 3.5 x 17.8 x 2e-07 mm, 1 faces, 0 solids (baked)
FEATURE [Part::Revolution] Revolve064  label="removeToCreateScrewAndThreadedInsertHole003"
  Angle = 360
  Axis = (0,1,0)
  Base = (0,0,0)
  FaceMakerClass = Part::FaceMakerBullseye
  Placement = pos=(89.5,0,3.5) rot=(0,0,1;0rad)
  Solid = false
  Source = -> Face060
  Symmetric = false
FEATURE [Part::Feature] Face061
  shape: bbox 3.5 x 17.8 x 2e-07 mm, 1 faces, 0 solids (baked)
FEATURE [Part::Revolution] Revolve065  label="removeToCreateScrewAndThreadedInsertHole004"
  Angle = 360
  Axis = (0,1,0)
  Base = (0,0,0)
  FaceMakerClass = Part::FaceMakerBullseye
  Placement = pos=(102.5,4.7,3.5) rot=(0,0,1;0rad)
  Solid = false
  Source = -> Face061
  Symmetric = false
FEATURE [Part::Feature] Face062
  shape: bbox 3.5 x 17.8 x 2e-07 mm, 1 faces, 0 solids (baked)
FEATURE [Part::Revolution] Revolve066  label="removeToCreateScrewAndThreadedInsertHole005"
  Angle = 360
  Axis = (0,1,0)
  Base = (0,0,0)
  FaceMakerClass = Part::FaceMakerBullseye
  Placement = pos=(102.5,4.7,68.5) rot=(0,0,1;0rad)
  Solid = false
  Source = -> Face062
  Symmetric = false
FEATURE [Part::MultiFuse] Fusion047  label="makeHoles"
  Shapes = -> [Revolve066,Revolve065,Revolve064,Revolve063,Revolve062,Revolve061]
FEATURE [Part::Feature] Face063
  shape: bbox 3.6 x 3.2 x 2e-07 mm, 1 faces, 0 solids (baked)
FEATURE [Part::Revolution] Revolve067  label="moreFrontCaseScrewRetainer002"
  Angle = 360
  Axis = (0,1,0)
  Base = (0,0,0)
  FaceMakerClass = Part::FaceMakerBullseye
  Placement = pos=(102.5,4.5,68.5) rot=(0,0,1;0rad)
  Solid = false
  Source = -> Face063
  Symmetric = false
FEATURE [Part::Feature] Face064
  shape: bbox 3.6 x 3.2 x 2e-07 mm, 1 faces, 0 solids (baked)
FEATURE [Part::Revolution] Revolve068  label="moreFrontCaseScrewRetainer003"
  Angle = 360
  Axis = (0,1,0)
  Base = (0,0,0)
  FaceMakerClass = Part::FaceMakerBullseye
  Placement = pos=(102.5,4.5,3.5) rot=(0,0,1;0rad)
  Solid = false
  Source = -> Face064
  Symmetric = false
FEATURE [Part::Cut] Cut014  label="bottom003"
  Base = -> Cut007
  Tool = -> Fusion047
FEATURE [Part::Feature] Face065
  shape: bbox 3.5 x 17.8 x 2e-07 mm, 1 faces, 0 solids (baked)
FEATURE [Part::Revolution] Revolve069  label="removeToCreateScrewAndThreadedInsertHole006"
  Angle = 360
  Axis = (0,1,0)
  Base = (0,0,0)
  FaceMakerClass = Part::FaceMakerBullseye
  Placement = pos=(12.5,0,10) rot=(0,0,1;0rad)
  Solid = false
  Source = -> Face065
  Symmetric = false
FEATURE [Part::Feature] Face066
  shape: bbox 3.5 x 17.8 x 2e-07 mm, 1 faces, 0 solids (baked)
FEATURE [Part::Revolution] Revolve070  label="removeToCreateScrewAndThreadedInsertHole007"
  Angle = 360
  Axis = (0,1,0)
  Base = (0,0,0)
  FaceMakerClass = Part::FaceMakerBullseye
  Placement = pos=(12.5,0,62) rot=(0,0,1;0rad)
  Solid = false
  Source = -> Face066
  Symmetric = false
FEATURE [Part::Feature] Face067
  shape: bbox 3.5 x 17.8 x 2e-07 mm, 1 faces, 0 solids (baked)
FEATURE [Part::Revolution] Revolve071  label="removeToCreateScrewAndThreadedInsertHole008"
  Angle = 360
  Axis = (0,1,0)
  Base = (0,0,0)
  FaceMakerClass = Part::FaceMakerBullseye
  Placement = pos=(89.5,0,68.5) rot=(0,0,1;0rad)
  Solid = false
  Source = -> Face067
  Symmetric = false
FEATURE [Part::Feature] Face068
  shape: bbox 3.5 x 17.8 x 2e-07 mm, 1 faces, 0 solids (baked)
FEATURE [Part::Revolution] Revolve072  label="removeToCreateScrewAndThreadedInsertHole009"
  Angle = 360
  Axis = (0,1,0)
  Base = (0,0,0)
  FaceMakerClass = Part::FaceMakerBullseye
  Placement = pos=(89.5,0,3.5) rot=(0,0,1;0rad)
  Solid = false
  Source = -> Face068
  Symmetric = false
FEATURE [Part::Feature] Face069
  shape: bbox 3.5 x 17.8 x 2e-07 mm, 1 faces, 0 solids (baked)
FEATURE [Part::Feature] Face070
  shape: bbox 3.5 x 17.8 x 2e-07 mm, 1 faces, 0 solids (baked)
FEATURE [Part::Revolution] Revolve073  label="removeToCreateScrewAndThreadedInsertHole010"
  Angle = 360
  Axis = (0,1,0)
  Base = (0,0,0)
  FaceMakerClass = Part::FaceMakerBullseye
  Placement = pos=(102.5,4.7,3.5) rot=(0,0,1;0rad)
  Solid = false
  Source = -> Face069
  Symmetric = false
FEATURE [Part::Revolution] Revolve074  label="removeToCreateScrewAndThreadedInsertHole011"
  Angle = 360
  Axis = (0,1,0)
  Base = (0,0,0)
  FaceMakerClass = Part::FaceMakerBullseye
  Placement = pos=(102.5,4.7,68.5) rot=(0,0,1;0rad)
  Solid = false
  Source = -> Face070
  Symmetric = false
FEATURE [Part::MultiFuse] Fusion048  label="makeHoles001"
  Shapes = -> [Revolve074,Revolve073,Revolve072,Revolve071,Revolve070,Revolve069]
FEATURE [Part::MultiFuse] Fusion049  label="caseScrewRetainers"
  Shapes = -> [Revolve067,Revolve068,Revolve048,Revolve047,Revolve039,Revolve040]
FEATURE [Part::Cut] Cut015  label="caseScrewRetainers001"
  Base = -> Fusion049
  Tool = -> Fusion048
FEATURE [Part::MultiFuse] Fusion050  label="casePillars"
  Shapes = -> [Revolve055,Revolve054,Revolve043,Revolve046,Revolve059,Revolve060]
FEATURE [Part::Feature] Face071 .. Face076  x6 (patterned run collapsed; names and placements below)
  shape: bbox 3.5 x 17.8 x 2e-07 mm, 1 faces, 0 solids (baked)
FEATURE [Part::Revolution] Revolve075  label="removeToCreateScrewAndThreadedInsertHole012"
  Angle = 360
  Axis = (0,1,0)
  Base = (0,0,0)
  FaceMakerClass = Part::FaceMakerBullseye
  Placement = pos=(12.5,0,10) rot=(0,0,1;0rad)
  Solid = false
  Source = -> Face071
  Symmetric = false
FEATURE [Part::Revolution] Revolve076  label="removeToCreateScrewAndThreadedInsertHole013"
  Angle = 360
  Axis = (0,1,0)
  Base = (0,0,0)
  FaceMakerClass = Part::FaceMakerBullseye
  Placement = pos=(12.5,0,62) rot=(0,0,1;0rad)
  Solid = false
  Source = -> Face072
  Symmetric = false
FEATURE [Part::Revolution] Revolve077  label="removeToCreateScrewAndThreadedInsertHole014"
  Angle = 360
  Axis = (0,1,0)
  Base = (0,0,0)
  FaceMakerClass = Part::FaceMakerBullseye
  Placement = pos=(89.5,0,68.5) rot=(0,0,1;0rad)
  Solid = false
  Source = -> Face073
  Symmetric = false
FEATURE [Part::Revolution] Revolve078  label="removeToCreateScrewAndThreadedInsertHole015"
  Angle = 360
  Axis = (0,1,0)
  Base = (0,0,0)
  FaceMakerClass = Part::FaceMakerBullseye
  Placement = pos=(89.5,0,3.5) rot=(0,0,1;0rad)
  Solid = false
  Source = -> Face074
  Symmetric = false
FEATURE [Part::Revolution] Revolve079  label="removeToCreateScrewAndThreadedInsertHole016"
  Angle = 360
  Axis = (0,1,0)
  Base = (0,0,0)
  FaceMakerClass = Part::FaceMakerBullseye
  Placement = pos=(102.5,4.7,3.5) rot=(0,0,1;0rad)
  Solid = false
  Source = -> Face075
  Symmetric = false
FEATURE [Part::Revolution] Revolve080  label="removeToCreateScrewAndThreadedInsertHole017"
  Angle = 360
  Axis = (0,1,0)
  Base = (0,0,0)
  FaceMakerClass = Part::FaceMakerBullseye
  Placement = pos=(102.5,4.7,68.5) rot=(0,0,1;0rad)
  Solid = false
  Source = -> Face076
  Symmetric = false
FEATURE [Part::MultiFuse] Fusion051  label="makeHoles002"
  Shapes = -> [Revolve080,Revolve079,Revolve078,Revolve077,Revolve076,Revolve075]
FEATURE [Part::Cut] Cut016  label="caesPillars"
  Base = -> Fusion050
  Tool = -> Fusion051
FEATURE [Part::Revolution] Revolve009  label="plugHousing016"
  Angle = 360
  Axis = (0,1,0)
  Base = (0,0,0)
  FaceMakerClass = Part::FaceMakerBullseye
  Placement = pos=(0,0,36.15) rot=(0,0,1;0rad)
  Solid = false
  Source = -> Face012
  Symmetric = false
FEATURE [Part::MultiFuse] Fusion014  label="plugHousing023"
  Placement = pos=(0,0,0) rot=(0,0,1;1.5708rad)
  Shapes = -> [Revolve011,Revolve009]
FEATURE [Part::Revolution] Revolve010  label="plugHousing017"
  Angle = 360
  Axis = (0,1,0)
  Base = (0,0,0)
  FaceMakerClass = Part::FaceMakerBullseye
  Placement = pos=(0,0,36.15) rot=(0,0,1;0rad)
  Solid = false
  Source = -> Face014
  Symmetric = false
FEATURE [Part::MultiFuse] Fusion015  label="plugHousing024"
  Placement = pos=(0,0,0) rot=(0,0,1;1.5708rad)
  Shapes = -> [Revolve010,Revolve015]
FEATURE [Part::Revolution] Revolve014  label="plugHousing026"
  Angle = 360
  Axis = (0,1,0)
  Base = (0,0,0)
  FaceMakerClass = Part::FaceMakerBullseye
  Placement = pos=(0,0,36.15) rot=(0,0,1;0rad)
  Solid = false
  Source = -> Face011
  Symmetric = false
FEATURE [Part::Revolution] Revolve013  label="plugHousing025"
  Angle = 360
  Axis = (0,1,0)
  Base = (0,0,0)
  FaceMakerClass = Part::FaceMakerBullseye
  Placement = pos=(0,0,36.15) rot=(0,0,1;0rad)
  Solid = false
  Source = -> Face015
  Symmetric = false
FEATURE [Part::MultiFuse] Fusion016  label="plugHousing028"
  Placement = pos=(0,19,0) rot=(0,0,1;3.14159rad)
  Shapes = -> [Fusion014,Fusion013]
FEATURE [Part::MultiFuse] Fusion011  label="plugHousing018"
  Placement = pos=(0,0,0) rot=(0,0,1;1.5708rad)
  Shapes = -> [Revolve014,Revolve013]
FEATURE [Part::MultiFuse] Fusion012  label="plugHousing019"
  Placement = pos=(0,19,0) rot=(0,0,1;3.14159rad)
  Shapes = -> [Fusion011,Fusion015]
FEATURE [Part::MultiFuse] Fusion017  label="plugHousing029"
  Placement = pos=(122.621,0,-0.15) rot=(0,0,1;0rad)
  Shapes = -> [Fusion016,Fusion012]
FEATURE [Part::MultiFuse] Fusion052  label="casePillarRetainers"
  Shapes = -> [Extrude012,Extrude013,Extrude014,Extrude015,Extrude016,Extrude017,Extrude018,Extrude019,Box011,Box012]
FEATURE [Part::Feature] Face077
  shape: bbox 3.5 x 17.8 x 2e-07 mm, 1 faces, 0 solids (baked)
FEATURE [Part::Revolution] Revolve081  label="removeToCreateScrewAndThreadedInsertHole018"
  Angle = 360
  Axis = (0,1,0)
  Base = (0,0,0)
  FaceMakerClass = Part::FaceMakerBullseye
  Placement = pos=(62.3,30.3,19.7) rot=(0,0,1;0rad)
  Solid = false
  Source = -> Face077
  Symmetric = false
FEATURE [Part::Feature] Face078
  shape: bbox 3.5 x 17.8 x 2e-07 mm, 1 faces, 0 solids (baked)
FEATURE [Part::Revolution] Revolve082  label="removeToCreateScrewAndThreadedInsertHole019"
  Angle = 360
  Axis = (0,1,0)
  Base = (0,0,0)
  FaceMakerClass = Part::FaceMakerBullseye
  Placement = pos=(62.3,30.3,51.7) rot=(0,0,1;0rad)
  Solid = false
  Source = -> Face078
  Symmetric = false
FEATURE [Part::Feature] Face079
  shape: bbox 3.5 x 17.8 x 2e-07 mm, 1 faces, 0 solids (baked)
FEATURE [Part::Revolution] Revolve083  label="removeToCreateScrewAndThreadedInsertHole020"
  Angle = 360
  Axis = (0,1,0)
  Base = (0,0,0)
  FaceMakerClass = Part::FaceMakerBullseye
  Placement = pos=(30.3,30.3,19.7) rot=(0,0,1;0rad)
  Solid = false
  Source = -> Face079
  Symmetric = false
FEATURE [Part::Feature] Face080
  shape: bbox 3.5 x 17.8 x 2e-07 mm, 1 faces, 0 solids (baked)
FEATURE [Part::Revolution] Revolve084  label="removeToCreateScrewAndThreadedInsertHole021"
  Angle = 360
  Axis = (0,1,0)
  Base = (0,0,0)
  FaceMakerClass = Part::FaceMakerBullseye
  Placement = pos=(30.3,30.3,51.7) rot=(0,0,1;0rad)
  Solid = false
  Source = -> Face080
  Symmetric = false
FEATURE [Part::MultiFuse] Fusion053  label="createThreadedInsertHolesForFan"
  Shapes = -> [Revolve081,Revolve082,Revolve083,Revolve084]
FEATURE [Part::Cut] Cut017  label="fanScrewHousing001"
  Base = -> Fusion046
  Tool = -> Fusion053
FEATURE [Part::Feature] Face081
  shape: bbox 3.5 x 17.8 x 2e-07 mm, 1 faces, 0 solids (baked)
FEATURE [Part::Revolution] Revolve085  label="removeToCreateScrewAndThreadedInsertHole022"
  Angle = 360
  Axis = (0,1,0)
  Base = (0,0,0)
  FaceMakerClass = Part::FaceMakerBullseye
  Placement = pos=(62.3,30.3,19.7) rot=(0,0,1;0rad)
  Solid = false
  Source = -> Face081
  Symmetric = false
FEATURE [Part::Feature] Face082
  shape: bbox 3.5 x 17.8 x 2e-07 mm, 1 faces, 0 solids (baked)
FEATURE [Part::Revolution] Revolve086  label="removeToCreateScrewAndThreadedInsertHole023"
  Angle = 360
  Axis = (0,1,0)
  Base = (0,0,0)
  FaceMakerClass = Part::FaceMakerBullseye
  Placement = pos=(62.3,30.3,51.7) rot=(0,0,1;0rad)
  Solid = false
  Source = -> Face082
  Symmetric = false
FEATURE [Part::Feature] Face083
  shape: bbox 3.5 x 17.8 x 2e-07 mm, 1 faces, 0 solids (baked)
FEATURE [Part::Revolution] Revolve087  label="removeToCreateScrewAndThreadedInsertHole024"
  Angle = 360
  Axis = (0,1,0)
  Base = (0,0,0)
  FaceMakerClass = Part::FaceMakerBullseye
  Placement = pos=(30.3,30.3,19.7) rot=(0,0,1;0rad)
  Solid = false
  Source = -> Face083
  Symmetric = false
FEATURE [Part::Feature] Face084
  shape: bbox 3.5 x 17.8 x 2e-07 mm, 1 faces, 0 solids (baked)
FEATURE [Part::Revolution] Revolve088  label="removeToCreateScrewAndThreadedInsertHole025"
  Angle = 360
  Axis = (0,1,0)
  Base = (0,0,0)
  FaceMakerClass = Part::FaceMakerBullseye
  Placement = pos=(30.3,30.3,51.7) rot=(0,0,1;0rad)
  Solid = false
  Source = -> Face084
  Symmetric = false
FEATURE [Part::MultiFuse] Fusion054  label="createThreadedInsertHolesForFan001"
  Shapes = -> [Revolve085,Revolve086,Revolve087,Revolve088]
FEATURE [Part::Cut] Cut018  label="top007"
  Base = -> Fusion040
  Tool = -> Fusion054
FEATURE [Sketcher::SketchObject] Sketch029
  FullyConstrained = false
  Placement = pos=(0,0,0) rot=(-1,0,0;4.71239rad)
  sketch-geometry (58):
    g0: LineSegment StartX=0 StartY=0 StartZ=0 EndX=-38.2 EndY=0 EndZ=0
    g1: LineSegment StartX=0 StartY=0 StartZ=0 EndX=0 EndY=-38.2 EndZ=0
    g2: LineSegment StartX=0 StartY=-38.2 StartZ=0 EndX=-38.2 EndY=-38.2 EndZ=0
    g3: LineSegment StartX=-38.2 StartY=0 StartZ=0 EndX=-38.2 EndY=-38.2 EndZ=0
    g4: LineSegment StartX=-38.2 StartY=-38.2 StartZ=0 EndX=-35.7 EndY=-38.2 EndZ=0
    g5: LineSegment StartX=-38.2 StartY=0 StartZ=0 EndX=-35.7 EndY=0 EndZ=0
    g6: LineSegment StartX=0 StartY=0 StartZ=0 EndX=-2.5 EndY=0 EndZ=0
    g7: LineSegment StartX=0 StartY=-38.2 StartZ=0 EndX=-2.5 EndY=-38.2 EndZ=0
    g8: LineSegment StartX=-2.5 StartY=0 StartZ=0 EndX=-2.5 EndY=-9 EndZ=0
    g9: LineSegment StartX=-35.7 StartY=0 StartZ=0 EndX=-35.7 EndY=-9 EndZ=0
    g10: LineSegment StartX=-35.7 StartY=-38.2 StartZ=0 EndX=-35.7 EndY=-29.2 EndZ=0
    g11: LineSegment StartX=-2.5 StartY=-38.2 StartZ=0 EndX=-2.5 EndY=-29.2 EndZ=0
    g12: LineSegment StartX=-5.5 StartY=-10.5 StartZ=0 EndX=-4 EndY=-10.5 EndZ=0
    g13: LineSegment StartX=-4 StartY=-10.5 StartZ=0 EndX=-2.5 EndY=-10.5 EndZ=0
    g14: ArcOfCircle CenterX=-4 CenterY=-10.5 CenterZ=0 NormalX=0 NormalY=0 NormalZ=1 AngleXU=0 Radius=1.5 StartAngle=5e-16 EndAngle=3.14159
    g15: LineSegment StartX=-35.7 StartY=-9 StartZ=0 EndX=-35.7 EndY=-10.5 EndZ=0
    g16: LineSegment StartX=-32.7 StartY=-10.5 StartZ=0 EndX=-34.2 EndY=-10.5 EndZ=0
    g17: ArcOfCircle CenterX=-34.2 CenterY=-10.5 CenterZ=0 NormalX=0 NormalY=0 NormalZ=1 AngleXU=0 Radius=1.5 StartAngle=0 EndAngle=3.14159
    g18: LineSegment StartX=-2.5 StartY=-9 StartZ=0 EndX=-2.5 EndY=-10.5 EndZ=0
    g19: LineSegment StartX=-34.2 StartY=-10.5 StartZ=0 EndX=-35.7 EndY=-10.5 EndZ=0
    g20: LineSegment StartX=-32.7 StartY=-10.5 StartZ=0 EndX=-29.7 EndY=-10.5 EndZ=0
    g21: LineSegment StartX=-29.7 StartY=-10.5 StartZ=0 EndX=-26.7 EndY=-10.5 EndZ=0
    g22: LineSegment StartX=-26.7 StartY=-10.5 StartZ=0 EndX=-23.6 EndY=-10.5 EndZ=0
    g23: LineSegment StartX=-23.6 StartY=-10.5 StartZ=0 EndX=-20.6 EndY=-10.5 EndZ=0
    g24: LineSegment StartX=-20.6 StartY=-10.5 StartZ=0 EndX=-17.6 EndY=-10.5 EndZ=0
    g25: LineSegment StartX=-17.6 StartY=-10.5 StartZ=0 EndX=-14.6 EndY=-10.5 EndZ=0
    g26: LineSegment StartX=-14.6 StartY=-10.5 StartZ=0 EndX=-11.5 EndY=-10.5 EndZ=0
    g27: LineSegment StartX=-11.5 StartY=-10.5 StartZ=0 EndX=-8.5 EndY=-10.5 EndZ=0
    g28: LineSegment StartX=-8.5 StartY=-10.5 StartZ=0 EndX=-5.5 EndY=-10.5 EndZ=0
    g29: LineSegment StartX=-35.7 StartY=-10.5 StartZ=0 EndX=-35.7 EndY=-27.7 EndZ=0
    g30: LineSegment StartX=-2.5 StartY=-27.7 StartZ=0 EndX=-2.5 EndY=-10.5 EndZ=0
    g31: LineSegment StartX=-14.5 StartY=-10.5 StartZ=0 EndX=-11.5 EndY=-10.5 EndZ=0
    g32: ArcOfCircle CenterX=-34.2 CenterY=-27.7 CenterZ=0 NormalX=0 NormalY=0 NormalZ=1 AngleXU=0 Radius=1.5 StartAngle=3.14159 EndAngle=6.28319
    g33: LineSegment StartX=-35.7 StartY=-27.7 StartZ=0 EndX=-35.7 EndY=-29.2 EndZ=0
    g34: ArcOfCircle CenterX=-4 CenterY=-27.7 CenterZ=0 NormalX=0 NormalY=0 NormalZ=1 AngleXU=0 Radius=1.5 StartAngle=3.1416 EndAngle=6.28319
    g35: LineSegment StartX=-5.5 StartY=-27.7 StartZ=0 EndX=-5.5 EndY=-10.5 EndZ=0
    g36: LineSegment StartX=-38.2 StartY=0 StartZ=0 EndX=0 EndY=-38.2 EndZ=0
    g37: LineSegment StartX=-38.2 StartY=-38.2 StartZ=0 EndX=0 EndY=0 EndZ=0
    g38: Circle CenterX=-19.1993 CenterY=-19.1993 CenterZ=0 NormalX=0 NormalY=0 NormalZ=1 AngleXU=0 Radius=17.5127
    g39: LineSegment StartX=-11.5 StartY=-10.5 StartZ=0 EndX=-11.5 EndY=-4.3 EndZ=0
    g40: LineSegment StartX=-8.5 StartY=-10.5 StartZ=0 EndX=-8.5 EndY=-4.3 EndZ=0
    g41: LineSegment StartX=-14.6 StartY=-10.5 StartZ=0 EndX=-14.6 EndY=-1.8 EndZ=0
    g42: ArcOfCircle CenterX=-10 CenterY=-4.3 CenterZ=0 NormalX=0 NormalY=0 NormalZ=1 AngleXU=0 Radius=1.5 StartAngle=2e-16 EndAngle=3.14159
    g43: ArcOfCircle CenterX=-16.1 CenterY=-1.8 CenterZ=0 NormalX=0 NormalY=0 NormalZ=1 AngleXU=0 Radius=1.5 StartAngle=5e-16 EndAngle=3.14159
    g44: LineSegment StartX=-17.6 StartY=-10.5 StartZ=0 EndX=-17.6 EndY=-1.8 EndZ=0
    g45: LineSegment StartX=-20.6 StartY=-10.5 StartZ=0 EndX=-20.6 EndY=-1.8 EndZ=0
    g46: LineSegment StartX=-23.6 StartY=-10.5 StartZ=0 EndX=-23.6 EndY=-1.8 EndZ=0
    g47: ArcOfCircle CenterX=-22.1 CenterY=-1.8 CenterZ=0 NormalX=0 NormalY=0 NormalZ=1 AngleXU=0 Radius=1.5 StartAngle=5e-16 EndAngle=3.14159
    g48: LineSegment StartX=-26.7 StartY=-10.5 StartZ=0 EndX=-26.7 EndY=-4.3 EndZ=0
    g49: LineSegment StartX=-29.7 StartY=-10.5 StartZ=0 EndX=-29.7 EndY=-4.3 EndZ=0
    g50: ArcOfCircle CenterX=-28.2 CenterY=-4.3 CenterZ=0 NormalX=0 NormalY=0 NormalZ=1 AngleXU=0 Radius=1.5 StartAngle=2e-16 EndAngle=3.14159
    g51: LineSegment StartX=-29.7 StartY=-10.5 StartZ=0 EndX=-29.7 EndY=-27.7 EndZ=0
    g52: LineSegment StartX=-26.7 StartY=-10.5 StartZ=0 EndX=-26.7 EndY=-27.7 EndZ=0
    g53: LineSegment StartX=-23.6 StartY=-10.5 StartZ=0 EndX=-23.6 EndY=-27.7 EndZ=0
    g54: LineSegment StartX=-20.6 StartY=-10.5 StartZ=0 EndX=-20.6 EndY=-27.7 EndZ=0
    g55: LineSegment StartX=-32.7 StartY=-10.5 StartZ=0 EndX=-32.7 EndY=-27.7 EndZ=0
    g56: LineSegment StartX=-17.6 StartY=-10.5 StartZ=0 EndX=-17.6 EndY=-27.7 EndZ=0
    g57: LineSegment StartX=-14.6 StartY=-10.5 StartZ=0 EndX=-14.6 EndY=-27.7 EndZ=0
  constraints (163):
    c: Coincident(g0,g-1)
    c: Horizontal(g0)
    c: Distance(g0) = 38.2
    c: Coincident(g1,g0)
    c: Vertical(g1)
    c: Distance(g1) = 38.2
    c: Horizontal(g2)
    c: Equal(g0,g2) = 38.2
    c: Coincident(g2,g1)
    c: Vertical(g3)
    c: Equal(g1,g3) = 38.2
    c: Coincident(g3,g0)
    c: Horizontal(g4)
    c: Coincident(g4,g2)
    c: Horizontal(g5)
    c: Coincident(g5,g0)
    c: Horizontal(g6)
    c: Coincident(g6,g0)
    c: Horizontal(g7)
    c: Coincident(g7,g1)
    c: Coincident(g8,g6)
    c: Vertical(g8)
    c: Distance(g8) = 9
    c: Vertical(g9)
    c: Equal(g8,g9) = 9
    c: Coincident(g9,g5)
    c: Coincident(g10,g4)
    c: Vertical(g10)
    c: Distance(g10) = 9
    c: Vertical(g11)
    c: Equal(g10,g11) = 9
    c: Coincident(g11,g7)
    c: Block(g0)
    c: Block(g8)
    c: Block(g9)
    c: Block(g11)
    c: Block(g10)
    c: Horizontal(g12)
    c: Distance(g12) = 1.5
    c: Horizontal(g13)
    c: Equal(g12,g13) = 1.5
    c: Coincident(g13,g12)
    c: Coincident(g14,g12)
    c: Coincident(g14,g13)
    c: Block(g14)
    c: Coincident(g15,g9)
    c: Vertical(g15)
    c: Distance(g15) = 1.5
    c: Horizontal(g16)
    c: Coincident(g17,g16)
    c: Block(g17)
    c: Coincident(g18,g8)
    c: Coincident(g18,g13)
    c: Vertical(g18)
    c: Distance(g16) = 1.5
    c: Horizontal(g19)
    c: Equal(g16,g19) = 1.5
    c: Coincident(g19,g16)
    c: Horizontal(g20)
    c: Coincident(g20,g16)
    c: Horizontal(g21)
    c: Coincident(g21,g20)
    c: Horizontal(g22)
    c: Distance(g22) = 3.1
    c: Coincident(g22,g21)
    c: Horizontal(g23)
    c: Coincident(g23,g22)
    c: Horizontal(g24)
    c: Coincident(g24,g23)
    c: Horizontal(g25)
    c: Coincident(g25,g24)
    c: Horizontal(g26)
    c: Coincident(g26,g25)
    c: Horizontal(g27)
    c: Coincident(g27,g26)
    c: Distance(g26) = 3.1
    c: Coincident(g28,g27)
    c: Coincident(g28,g12)
    c: Horizontal(g28)
    c: Distance(g28) = 3
    c: Distance(g20) = 3
    c: Distance(g21) = 3
    c: Distance(g23) = 3
    c: Distance(g24) = 3
    c: Distance(g25) = 3
    c: Distance(g27) = 3
    c: Coincident(g29,g15)
    c: Vertical(g29)
    c: Distance(g10) = 9
    c: Distance(g10) = 9
    c: Distance(g9) = 9
    c: Coincident(g30,g13)
    c: Vertical(g30)
    c: Distance(g30) = 17.2
    c: Horizontal(g31)
    c: Equal(g27,g31) = 3
    c: Block(g29)
    c: Coincident(g33,g10)
    c: Vertical(g33)
    c: Block(g32)
    c: Block(g34)
    c: Coincident(g35,g34)
    c: Coincident(g35,g12)
    c: Vertical(g35)
    c: Coincident(g36,g0)
    c: Coincident(g36,g1)
    c: Coincident(g37,g2)
    c: Coincident(g37,g0)
    c: PointOnObject(g38,g37)
    c: PointOnObject(g12,g38)
    c: Coincident(g39,g26)
    c: Vertical(g39)
    c: Distance(g39) = 6.2
    c: Vertical(g40)
    c: Equal(g39,g40) = 5.5
    c: Coincident(g40,g27)
    c: Coincident(g41,g25)
    c: Vertical(g41)
    c: Distance(g41) = 8.7
    c: Block(g42)
    c: Coincident(g42,g40)
    c: Block(g43)
    c: Coincident(g43,g41)
    c: Vertical(g44)
    c: Equal(g41,g44) = 8.2
    c: Coincident(g44,g24)
    c: Vertical(g45)
    c: Equal(g41,g45) = 8.2
    c: Coincident(g45,g23)
    c: Vertical(g46)
    c: Equal(g41,g46) = 8.2
    c: Coincident(g46,g22)
    c: Block(g47)
    c: Coincident(g47,g45)
    c: Vertical(g48)
    c: Coincident(g48,g21)
    c: Vertical(g49)
    c: Coincident(g49,g20)
    c: Block(g48)
    c: Block(g49)
    c: Block(g50)
    c: Coincident(g50,g48)
    c: Vertical(g51)
    c: Block(g51)
    c: Coincident(g51,g20)
    c: Vertical(g52)
    c: Block(g52)
    c: Coincident(g52,g21)
    c: Vertical(g53)
    c: Block(g53)
    c: Coincident(g53,g22)
    c: Vertical(g54)
    c: Block(g54)
    c: Coincident(g54,g23)
    c: Vertical(g55)
    c: Block(g55)
    c: Coincident(g55,g16)
    c: Vertical(g56)
    c: Block(g56)
    c: Coincident(g56,g24)
    c: Vertical(g57)
    c: Block(g57)
    c: Coincident(g57,g25)
